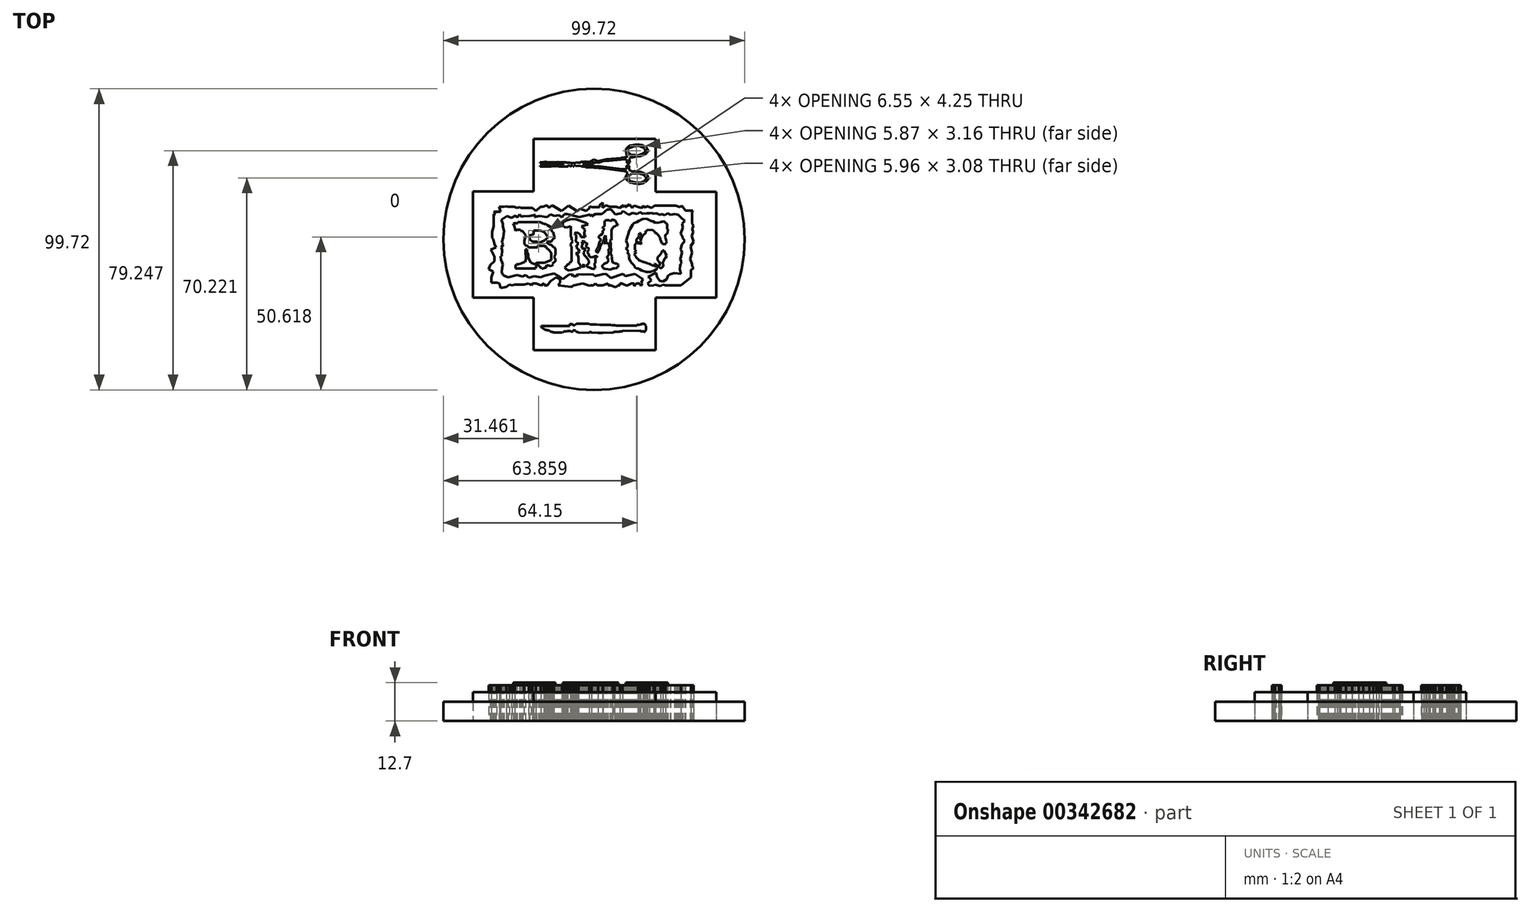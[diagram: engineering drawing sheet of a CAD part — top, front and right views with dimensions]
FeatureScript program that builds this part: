
annotation { "Feature Type Name" : "Feature", "Feature Type Description" : "" }
export const myFeature = defineFeature(function(context is Context, id is Id, definition is map)
    precondition{}
    {
        {
            var Q0;
            Q0=qCreatedBy(makeId("Top.planeOp"),FACE);
            var sketch = newSketch(context, id + "F0", { "sketchPlane" : qUnion([Q0])});
            skCircle(sketch, "E0", {"center": v(0, 0) * mm, "radius": 49.86 * mm});
            skSolve(sketch);
        }
        {
            var Q0;
            Q0=qCreatedBy(makeId("Top.planeOp"),FACE);
            var sketch = newSketch(context, id + "F1", { "sketchPlane" : qUnion([Q0])});
            skLineSegment(sketch, "E1", {"start": v(-40.1, 15.85) * mm, "end": v(-20.03, 15.85) * mm});
            skLineSegment(sketch, "E2", {"start": v(-20.03, 15.85) * mm, "end": v(-20.03, 33.22) * mm});
            skLineSegment(sketch, "E3", {"start": v(-20.03, 33.22) * mm, "end": v(20.4, 33.22) * mm});
            skLineSegment(sketch, "E4", {"start": v(20.4, 33.22) * mm, "end": v(20.4, 15.76) * mm});
            skLineSegment(sketch, "E5", {"start": v(20.4, 15.76) * mm, "end": v(40.46, 15.76) * mm});
            skLineSegment(sketch, "E6", {"start": v(40.46, 15.76) * mm, "end": v(40.46, -19.25) * mm});
            skLineSegment(sketch, "E7", {"start": v(40.46, -19.25) * mm, "end": v(20.4, -19.25) * mm});
            skLineSegment(sketch, "E8", {"start": v(20.4, -19.25) * mm, "end": v(20.4, -36.7) * mm});
            skLineSegment(sketch, "E9", {"start": v(20.4, -36.7) * mm, "end": v(-20.03, -36.7) * mm});
            skLineSegment(sketch, "E10", {"start": v(-20.03, -36.7) * mm, "end": v(-20.03, -19.25) * mm});
            skLineSegment(sketch, "E11", {"start": v(-20.03, -19.25) * mm, "end": v(-40.05, -19.25) * mm});
            skLineSegment(sketch, "E12", {"start": v(-40.05, -19.25) * mm, "end": v(-40.1, 15.85) * mm});
            skSolve(sketch);
        }
        {
            var Q0;
            Q0=qCreatedBy(makeId("Top.planeOp"),FACE);
            var sketch = newSketch(context, id + "F2", { "sketchPlane" : qUnion([Q0])});
            skLineSegment(sketch, "E13", {"start": v(-17.84, 25.58) * mm, "end": v(-17.84, 25.27) * mm});
            skLineSegment(sketch, "E14", {"start": v(-17.84, 25.27) * mm, "end": v(-16.2, 25.27) * mm});
            skLineSegment(sketch, "E15", {"start": v(-16.2, 25.27) * mm, "end": v(-16.2, 25.13) * mm});
            skLineSegment(sketch, "E16", {"start": v(-16.2, 25.13) * mm, "end": v(-15.9, 25.13) * mm});
            skLineSegment(sketch, "E17", {"start": v(-15.9, 25.13) * mm, "end": v(-15.76, 25.27) * mm});
            skLineSegment(sketch, "E18", {"start": v(-15.76, 25.27) * mm, "end": v(-15.26, 25.27) * mm});
            skLineSegment(sketch, "E19", {"start": v(-15.26, 25.27) * mm, "end": v(-15.26, 25.13) * mm});
            skLineSegment(sketch, "E20", {"start": v(-15.26, 25.13) * mm, "end": v(-12.92, 25.13) * mm});
            skLineSegment(sketch, "E21", {"start": v(-12.92, 25.13) * mm, "end": v(-12.8, 25) * mm});
            skLineSegment(sketch, "E22", {"start": v(-12.8, 25) * mm, "end": v(-12.56, 25) * mm});
            skLineSegment(sketch, "E23", {"start": v(-12.56, 25) * mm, "end": v(-12.56, 25.13) * mm});
            skLineSegment(sketch, "E24", {"start": v(-12.56, 25.13) * mm, "end": v(-12.27, 25) * mm});
            skLineSegment(sketch, "E25", {"start": v(-12.27, 25) * mm, "end": v(-12.15, 25) * mm});
            skLineSegment(sketch, "E26", {"start": v(-12.15, 25) * mm, "end": v(-9.99, 25) * mm});
            skLineSegment(sketch, "E27", {"start": v(-9.99, 25) * mm, "end": v(-9.99, 24.86) * mm});
            skLineSegment(sketch, "E28", {"start": v(-9.99, 24.86) * mm, "end": v(-10.34, 24.86) * mm});
            skLineSegment(sketch, "E29", {"start": v(-10.34, 24.86) * mm, "end": v(-11.16, 24.7) * mm});
            skLineSegment(sketch, "E30", {"start": v(-11.16, 24.7) * mm, "end": v(-11.19, 24.85) * mm});
            skLineSegment(sketch, "E31", {"start": v(-11.19, 24.85) * mm, "end": v(-11.41, 24.8) * mm});
            skLineSegment(sketch, "E32", {"start": v(-11.41, 24.8) * mm, "end": v(-11.86, 24.7) * mm});
            skLineSegment(sketch, "E33", {"start": v(-11.86, 24.7) * mm, "end": v(-11.89, 24.8) * mm});
            skLineSegment(sketch, "E34", {"start": v(-11.89, 24.8) * mm, "end": v(-12.03, 24.77) * mm});
            skLineSegment(sketch, "E35", {"start": v(-12.03, 24.77) * mm, "end": v(-12.56, 24.77) * mm});
            skLineSegment(sketch, "E36", {"start": v(-12.56, 24.77) * mm, "end": v(-12.8, 24.77) * mm});
            skLineSegment(sketch, "E37", {"start": v(-12.8, 24.77) * mm, "end": v(-12.8, 24.54) * mm});
            skLineSegment(sketch, "E38", {"start": v(-12.8, 24.54) * mm, "end": v(-13.2, 24.54) * mm});
            skLineSegment(sketch, "E39", {"start": v(-13.2, 24.54) * mm, "end": v(-13.2, 24.7) * mm});
            skLineSegment(sketch, "E40", {"start": v(-13.2, 24.7) * mm, "end": v(-13.43, 24.7) * mm});
            skLineSegment(sketch, "E41", {"start": v(-14.94, 24.58) * mm, "end": v(-13.43, 24.7) * mm});
            skLineSegment(sketch, "E42", {"start": v(-15.14, 24.58) * mm, "end": v(-14.94, 24.58) * mm});
            skLineSegment(sketch, "E43", {"start": v(-15.14, 24.58) * mm, "end": v(-15.13, 24.4) * mm});
            skLineSegment(sketch, "E44", {"start": v(-15.13, 24.4) * mm, "end": v(-15.3, 24.4) * mm});
            skLineSegment(sketch, "E45", {"start": v(-15.3, 24.4) * mm, "end": v(-15.31, 24.58) * mm});
            skLineSegment(sketch, "E46", {"start": v(-15.31, 24.58) * mm, "end": v(-15.58, 24.56) * mm});
            skLineSegment(sketch, "E47", {"start": v(-15.58, 24.56) * mm, "end": v(-15.57, 24.4) * mm});
            skLineSegment(sketch, "E48", {"start": v(-15.57, 24.4) * mm, "end": v(-15.9, 24.37) * mm});
            skLineSegment(sketch, "E49", {"start": v(-15.9, 24.37) * mm, "end": v(-15.92, 24.58) * mm});
            skLineSegment(sketch, "E50", {"start": v(-15.92, 24.58) * mm, "end": v(-16.2, 24.56) * mm});
            skLineSegment(sketch, "E51", {"start": v(-16.2, 24.56) * mm, "end": v(-16.34, 24.4) * mm});
            skLineSegment(sketch, "E52", {"start": v(-16.34, 24.4) * mm, "end": v(-17.87, 24.4) * mm});
            skLineSegment(sketch, "E53", {"start": v(-17.87, 24.4) * mm, "end": v(-17.84, 24.11) * mm});
            skLineSegment(sketch, "E54", {"start": v(-17.84, 24.11) * mm, "end": v(-15.14, 24.11) * mm});
            skLineSegment(sketch, "E55", {"start": v(-15.14, 24.11) * mm, "end": v(-14.67, 24.15) * mm});
            skLineSegment(sketch, "E56", {"start": v(-14.67, 24.15) * mm, "end": v(-14.53, 24.11) * mm});
            skLineSegment(sketch, "E57", {"start": v(-14.53, 24.11) * mm, "end": v(-14.12, 24.11) * mm});
            skLineSegment(sketch, "E58", {"start": v(-14.12, 24.11) * mm, "end": v(-13.84, 24.13) * mm});
            skLineSegment(sketch, "E59", {"start": v(-13.84, 24.13) * mm, "end": v(-12.97, 24.2) * mm});
            skLineSegment(sketch, "E60", {"start": v(-12.97, 24.2) * mm, "end": v(-12.56, 24.11) * mm});
            skLineSegment(sketch, "E61", {"start": v(-12.56, 24.11) * mm, "end": v(-12.39, 24.2) * mm});
            skLineSegment(sketch, "E62", {"start": v(-12.39, 24.2) * mm, "end": v(-11.57, 24.27) * mm});
            skLineSegment(sketch, "E63", {"start": v(-11.57, 24.27) * mm, "end": v(-11.56, 24.11) * mm});
            skLineSegment(sketch, "E64", {"start": v(-11.56, 24.11) * mm, "end": v(-11.29, 24.13) * mm});
            skLineSegment(sketch, "E65", {"start": v(-11.29, 24.13) * mm, "end": v(-11.16, 24.14) * mm});
            skLineSegment(sketch, "E66", {"start": v(-11.16, 24.14) * mm, "end": v(-8.61, 24.14) * mm});
            skLineSegment(sketch, "E67", {"start": v(-8.61, 24.14) * mm, "end": v(-8.61, 24.42) * mm});
            skLineSegment(sketch, "E68", {"start": v(-8.61, 24.42) * mm, "end": v(-8.03, 24.47) * mm});
            skLineSegment(sketch, "E69", {"start": v(-8.03, 24.47) * mm, "end": v(-8, 24.2) * mm});
            skLineSegment(sketch, "E70", {"start": v(-8, 24.2) * mm, "end": v(-7.59, 24.23) * mm});
            skLineSegment(sketch, "E71", {"start": v(-7.59, 24.23) * mm, "end": v(-7.6, 24.42) * mm});
            skLineSegment(sketch, "E72", {"start": v(-7.6, 24.42) * mm, "end": v(-6.99, 24.47) * mm});
            skLineSegment(sketch, "E73", {"start": v(-6.99, 24.47) * mm, "end": v(-6.96, 24.13) * mm});
            skLineSegment(sketch, "E74", {"start": v(-6.96, 24.13) * mm, "end": v(-6.64, 24.16) * mm});
            skLineSegment(sketch, "E75", {"start": v(-6.64, 24.16) * mm, "end": v(-6.67, 24.47) * mm});
            skLineSegment(sketch, "E76", {"start": v(-6.67, 24.47) * mm, "end": v(-6.1, 24.51) * mm});
            skLineSegment(sketch, "E77", {"start": v(-6.1, 24.51) * mm, "end": v(-6.08, 24.2) * mm});
            skLineSegment(sketch, "E78", {"start": v(-6.08, 24.2) * mm, "end": v(-4.47, 24.33) * mm});
            skLineSegment(sketch, "E79", {"start": v(-4.47, 24.33) * mm, "end": v(-4.1, 24.11) * mm});
            skLineSegment(sketch, "E80", {"start": v(-4.1, 24.11) * mm, "end": v(-3.34, 24.17) * mm});
            skLineSegment(sketch, "E81", {"start": v(-3.34, 24.17) * mm, "end": v(-2.81, 24.11) * mm});
            skLineSegment(sketch, "E82", {"start": v(-2.81, 24.11) * mm, "end": v(-2.25, 23.79) * mm});
            skLineSegment(sketch, "E83", {"start": v(-2.25, 23.79) * mm, "end": v(-1.73, 23.94) * mm});
            skLineSegment(sketch, "E84", {"start": v(-1.73, 23.94) * mm, "end": v(3.2, 23.51) * mm});
            skLineSegment(sketch, "E85", {"start": v(3.2, 23.51) * mm, "end": v(10.9, 22.47) * mm});
            skLineSegment(sketch, "E86", {"start": v(10.9, 22.47) * mm, "end": v(10.95, 21.79) * mm});
            skLineSegment(sketch, "E87", {"start": v(10.95, 21.79) * mm, "end": v(10.97, 21.58) * mm});
            skLineSegment(sketch, "E88", {"start": v(10.95, 21.4) * mm, "end": v(10.97, 21.58) * mm});
            skLineSegment(sketch, "E89", {"start": v(10.95, 21.4) * mm, "end": v(10.63, 21.17) * mm});
            skLineSegment(sketch, "E90", {"start": v(10.63, 21.17) * mm, "end": v(10.65, 20.91) * mm});
            skLineSegment(sketch, "E91", {"start": v(10.65, 20.91) * mm, "end": v(10.57, 20.78) * mm});
            skLineSegment(sketch, "E92", {"start": v(10.57, 20.78) * mm, "end": v(10.47, 20.6) * mm});
            skLineSegment(sketch, "E93", {"start": v(10.47, 20.6) * mm, "end": v(10.49, 20.35) * mm});
            skLineSegment(sketch, "E94", {"start": v(10.49, 20.35) * mm, "end": v(10.73, 19.85) * mm});
            skLineSegment(sketch, "E95", {"start": v(10.73, 19.85) * mm, "end": v(11.48, 19.2) * mm});
            skLineSegment(sketch, "E96", {"start": v(11.48, 19.2) * mm, "end": v(12.13, 18.83) * mm});
            skLineSegment(sketch, "E97", {"start": v(12.13, 18.83) * mm, "end": v(13.3, 18.5) * mm});
            skLineSegment(sketch, "E98", {"start": v(13.3, 18.5) * mm, "end": v(14.8, 18.32) * mm});
            skLineSegment(sketch, "E99", {"start": v(14.8, 18.32) * mm, "end": v(16.04, 18.5) * mm});
            skLineSegment(sketch, "E100", {"start": v(16.04, 18.5) * mm, "end": v(17.27, 19.24) * mm});
            skLineSegment(sketch, "E101", {"start": v(17.27, 19.24) * mm, "end": v(17.88, 19.85) * mm});
            skLineSegment(sketch, "E102", {"start": v(17.88, 19.85) * mm, "end": v(17.98, 20.07) * mm});
            skLineSegment(sketch, "E103", {"start": v(17.98, 20.07) * mm, "end": v(18.03, 20.2) * mm});
            skLineSegment(sketch, "E104", {"start": v(18.03, 20.2) * mm, "end": v(17.85, 20.76) * mm});
            skLineSegment(sketch, "E105", {"start": v(17.85, 20.76) * mm, "end": v(17.56, 21.29) * mm});
            skLineSegment(sketch, "E106", {"start": v(17.56, 21.29) * mm, "end": v(16.09, 22.14) * mm});
            skLineSegment(sketch, "E107", {"start": v(16.09, 22.14) * mm, "end": v(15.92, 22.1) * mm});
            skLineSegment(sketch, "E108", {"start": v(15.92, 22.1) * mm, "end": v(15.63, 22.23) * mm});
            skLineSegment(sketch, "E109", {"start": v(15.63, 22.23) * mm, "end": v(15.4, 22.34) * mm});
            skLineSegment(sketch, "E110", {"start": v(15.4, 22.34) * mm, "end": v(15.22, 22.37) * mm});
            skLineSegment(sketch, "E111", {"start": v(15.22, 22.37) * mm, "end": v(14.23, 22.47) * mm});
            skLineSegment(sketch, "E112", {"start": v(14.23, 22.47) * mm, "end": v(13.87, 22.47) * mm});
            skLineSegment(sketch, "E113", {"start": v(13.87, 22.47) * mm, "end": v(13.34, 22.6) * mm});
            skLineSegment(sketch, "E114", {"start": v(13.34, 22.6) * mm, "end": v(12.58, 22.47) * mm});
            skLineSegment(sketch, "E115", {"start": v(12.58, 22.47) * mm, "end": v(12.52, 22.58) * mm});
            skLineSegment(sketch, "E116", {"start": v(12.52, 22.58) * mm, "end": v(12.46, 22.7) * mm});
            skLineSegment(sketch, "E117", {"start": v(12.46, 22.7) * mm, "end": v(12.12, 22.67) * mm});
            skLineSegment(sketch, "E118", {"start": v(12.12, 22.67) * mm, "end": v(11.64, 23.1) * mm});
            skLineSegment(sketch, "E119", {"start": v(11.64, 23.1) * mm, "end": v(11.64, 24.33) * mm});
            skLineSegment(sketch, "E120", {"start": v(11.64, 24.33) * mm, "end": v(11.3, 24.53) * mm});
            skLineSegment(sketch, "E121", {"start": v(11.3, 24.53) * mm, "end": v(10.97, 24.5) * mm});
            skLineSegment(sketch, "E122", {"start": v(10.97, 24.5) * mm, "end": v(10.79, 24.2) * mm});
            skLineSegment(sketch, "E123", {"start": v(10.79, 24.2) * mm, "end": v(10.85, 23.41) * mm});
            skLineSegment(sketch, "E124", {"start": v(10.85, 23.41) * mm, "end": v(10.65, 23.49) * mm});
            skLineSegment(sketch, "E125", {"start": v(10.65, 23.49) * mm, "end": v(10.53, 23.28) * mm});
            skLineSegment(sketch, "E126", {"start": v(10.53, 23.28) * mm, "end": v(10.38, 23.28) * mm});
            skLineSegment(sketch, "E127", {"start": v(10.38, 23.28) * mm, "end": v(9.3, 23.2) * mm});
            skLineSegment(sketch, "E128", {"start": v(9.3, 23.2) * mm, "end": v(1.17, 24.2) * mm});
            skLineSegment(sketch, "E129", {"start": v(1.17, 24.2) * mm, "end": v(0.02, 24.11) * mm});
            skLineSegment(sketch, "E130", {"start": v(0.02, 24.11) * mm, "end": v(0, 24.33) * mm});
            skLineSegment(sketch, "E131", {"start": v(0, 24.33) * mm, "end": v(-0.25, 24.47) * mm});
            skLineSegment(sketch, "E132", {"start": v(-0.25, 24.47) * mm, "end": v(-2.08, 24.58) * mm});
            skLineSegment(sketch, "E133", {"start": v(-2.08, 24.58) * mm, "end": v(-2.6, 24.64) * mm});
            skLineSegment(sketch, "E134", {"start": v(-2.6, 24.64) * mm, "end": v(-2.82, 24.77) * mm});
            skLineSegment(sketch, "E135", {"start": v(-2.82, 24.77) * mm, "end": v(-3.17, 24.74) * mm});
            skLineSegment(sketch, "E136", {"start": v(-3.17, 24.74) * mm, "end": v(-3.8, 25) * mm});
            skLineSegment(sketch, "E137", {"start": v(-3.8, 25) * mm, "end": v(-2.9, 25.06) * mm});
            skLineSegment(sketch, "E138", {"start": v(-2.9, 25.06) * mm, "end": v(-1.6, 25.18) * mm});
            skLineSegment(sketch, "E139", {"start": v(-1.6, 25.18) * mm, "end": v(-1.32, 25.32) * mm});
            skLineSegment(sketch, "E140", {"start": v(-1.32, 25.32) * mm, "end": v(-0.37, 25.43) * mm});
            skLineSegment(sketch, "E141", {"start": v(-0.37, 25.43) * mm, "end": v(0.27, 25.46) * mm});
            skLineSegment(sketch, "E142", {"start": v(0.27, 25.46) * mm, "end": v(0.72, 25.6) * mm});
            skLineSegment(sketch, "E143", {"start": v(0.72, 25.6) * mm, "end": v(1.53, 25.46) * mm});
            skLineSegment(sketch, "E144", {"start": v(1.53, 25.46) * mm, "end": v(2.25, 25.64) * mm});
            skLineSegment(sketch, "E145", {"start": v(2.25, 25.64) * mm, "end": v(3.02, 25.86) * mm});
            skLineSegment(sketch, "E146", {"start": v(3.02, 25.86) * mm, "end": v(4.96, 26.04) * mm});
            skLineSegment(sketch, "E147", {"start": v(4.96, 26.04) * mm, "end": v(10.32, 26.5) * mm});
            skLineSegment(sketch, "E148", {"start": v(10.32, 26.5) * mm, "end": v(10.84, 26.22) * mm});
            skLineSegment(sketch, "E149", {"start": v(10.84, 26.22) * mm, "end": v(10.84, 25.46) * mm});
            skLineSegment(sketch, "E150", {"start": v(10.84, 25.46) * mm, "end": v(11.2, 25.1) * mm});
            skLineSegment(sketch, "E151", {"start": v(11.2, 25.1) * mm, "end": v(11.83, 25.36) * mm});
            skLineSegment(sketch, "E152", {"start": v(11.83, 25.36) * mm, "end": v(11.67, 26.72) * mm});
            skLineSegment(sketch, "E153", {"start": v(11.67, 26.72) * mm, "end": v(11.83, 26.97) * mm});
            skLineSegment(sketch, "E154", {"start": v(11.83, 26.97) * mm, "end": v(11.94, 27.08) * mm});
            skLineSegment(sketch, "E155", {"start": v(11.94, 27.08) * mm, "end": v(12.2, 27.22) * mm});
            skLineSegment(sketch, "E156", {"start": v(12.2, 27.22) * mm, "end": v(12.78, 27.22) * mm});
            skLineSegment(sketch, "E157", {"start": v(12.78, 27.22) * mm, "end": v(13.36, 27.3) * mm});
            skLineSegment(sketch, "E158", {"start": v(13.36, 27.3) * mm, "end": v(14.32, 27.38) * mm});
            skLineSegment(sketch, "E159", {"start": v(14.32, 27.38) * mm, "end": v(15.05, 27.53) * mm});
            skLineSegment(sketch, "E160", {"start": v(15.05, 27.53) * mm, "end": v(15.33, 27.55) * mm});
            skLineSegment(sketch, "E161", {"start": v(15.33, 27.55) * mm, "end": v(15.52, 27.64) * mm});
            skLineSegment(sketch, "E162", {"start": v(15.52, 27.64) * mm, "end": v(16.3, 27.93) * mm});
            skLineSegment(sketch, "E163", {"start": v(16.3, 27.93) * mm, "end": v(16.45, 28.02) * mm});
            skLineSegment(sketch, "E164", {"start": v(16.45, 28.02) * mm, "end": v(16.58, 28.1) * mm});
            skLineSegment(sketch, "E165", {"start": v(16.58, 28.1) * mm, "end": v(17.17, 28.41) * mm});
            skLineSegment(sketch, "E166", {"start": v(17.17, 28.41) * mm, "end": v(17.3, 28.51) * mm});
            skLineSegment(sketch, "E167", {"start": v(17.3, 28.51) * mm, "end": v(17.67, 28.99) * mm});
            skLineSegment(sketch, "E168", {"start": v(17.67, 28.99) * mm, "end": v(17.81, 29.23) * mm});
            skLineSegment(sketch, "E169", {"start": v(17.81, 29.23) * mm, "end": v(17.82, 29.45) * mm});
            skLineSegment(sketch, "E170", {"start": v(17.82, 29.45) * mm, "end": v(17.17, 30.56) * mm});
            skLineSegment(sketch, "E171", {"start": v(17.17, 30.56) * mm, "end": v(17.06, 30.67) * mm});
            skLineSegment(sketch, "E172", {"start": v(17.06, 30.67) * mm, "end": v(16.87, 30.77) * mm});
            skLineSegment(sketch, "E173", {"start": v(16.87, 30.77) * mm, "end": v(16.68, 30.9) * mm});
            skLineSegment(sketch, "E174", {"start": v(16.68, 30.9) * mm, "end": v(16.37, 31.08) * mm});
            skLineSegment(sketch, "E175", {"start": v(16.37, 31.08) * mm, "end": v(16.23, 31.13) * mm});
            skLineSegment(sketch, "E176", {"start": v(16.23, 31.13) * mm, "end": v(16, 31.18) * mm});
            skLineSegment(sketch, "E177", {"start": v(16, 31.18) * mm, "end": v(15.8, 31.28) * mm});
            skLineSegment(sketch, "E178", {"start": v(15.8, 31.28) * mm, "end": v(15.5, 31.23) * mm});
            skLineSegment(sketch, "E179", {"start": v(15.5, 31.23) * mm, "end": v(15.2, 31.28) * mm});
            skLineSegment(sketch, "E180", {"start": v(15.2, 31.28) * mm, "end": v(14.87, 31.35) * mm});
            skLineSegment(sketch, "E181", {"start": v(14.87, 31.35) * mm, "end": v(14.74, 31.43) * mm});
            skLineSegment(sketch, "E182", {"start": v(14.74, 31.43) * mm, "end": v(13.85, 31.38) * mm});
            skLineSegment(sketch, "E183", {"start": v(13.85, 31.38) * mm, "end": v(13.62, 31.33) * mm});
            skLineSegment(sketch, "E184", {"start": v(13.62, 31.33) * mm, "end": v(13.3, 31.3) * mm});
            skLineSegment(sketch, "E185", {"start": v(13.3, 31.3) * mm, "end": v(13.07, 31.3) * mm});
            skLineSegment(sketch, "E186", {"start": v(13.07, 31.3) * mm, "end": v(12.73, 31.17) * mm});
            skLineSegment(sketch, "E187", {"start": v(12.73, 31.17) * mm, "end": v(12.4, 31.14) * mm});
            skLineSegment(sketch, "E188", {"start": v(12.4, 31.14) * mm, "end": v(12.17, 31.12) * mm});
            skLineSegment(sketch, "E189", {"start": v(12.17, 31.12) * mm, "end": v(11.53, 30.72) * mm});
            skLineSegment(sketch, "E190", {"start": v(11.53, 30.72) * mm, "end": v(11.2, 30.58) * mm});
            skLineSegment(sketch, "E191", {"start": v(11.2, 30.58) * mm, "end": v(11.07, 30.5) * mm});
            skLineSegment(sketch, "E192", {"start": v(11.07, 30.5) * mm, "end": v(10.73, 30.12) * mm});
            skLineSegment(sketch, "E193", {"start": v(10.73, 30.12) * mm, "end": v(10.56, 29.77) * mm});
            skLineSegment(sketch, "E194", {"start": v(10.56, 29.77) * mm, "end": v(10.45, 29.52) * mm});
            skLineSegment(sketch, "E195", {"start": v(10.45, 29.52) * mm, "end": v(10.46, 29.36) * mm});
            skLineSegment(sketch, "E196", {"start": v(10.46, 29.36) * mm, "end": v(10.52, 29.22) * mm});
            skLineSegment(sketch, "E197", {"start": v(10.52, 29.22) * mm, "end": v(10.56, 29) * mm});
            skLineSegment(sketch, "E198", {"start": v(10.56, 29) * mm, "end": v(10.52, 28.82) * mm});
            skLineSegment(sketch, "E199", {"start": v(10.52, 28.82) * mm, "end": v(10.72, 28.55) * mm});
            skLineSegment(sketch, "E200", {"start": v(10.72, 28.55) * mm, "end": v(10.79, 27.95) * mm});
            skLineSegment(sketch, "E201", {"start": v(10.79, 27.95) * mm, "end": v(11.06, 27.73) * mm});
            skLineSegment(sketch, "E202", {"start": v(11.06, 27.73) * mm, "end": v(11.1, 27.64) * mm});
            skLineSegment(sketch, "E203", {"start": v(11.1, 27.64) * mm, "end": v(10.67, 27.2) * mm});
            skLineSegment(sketch, "E204", {"start": v(10.67, 27.2) * mm, "end": v(10.07, 27.22) * mm});
            skLineSegment(sketch, "E205", {"start": v(10.07, 27.22) * mm, "end": v(10, 27.08) * mm});
            skLineSegment(sketch, "E206", {"start": v(10, 27.08) * mm, "end": v(9.13, 27.08) * mm});
            skLineSegment(sketch, "E207", {"start": v(9.13, 27.08) * mm, "end": v(8.94, 26.9) * mm});
            skLineSegment(sketch, "E208", {"start": v(8.94, 26.9) * mm, "end": v(4.28, 26.5) * mm});
            skLineSegment(sketch, "E209", {"start": v(4.28, 26.5) * mm, "end": v(4.27, 26.47) * mm});
            skLineSegment(sketch, "E210", {"start": v(4.27, 26.47) * mm, "end": v(4.15, 26.47) * mm});
            skLineSegment(sketch, "E211", {"start": v(4.15, 26.47) * mm, "end": v(4.27, 26.5) * mm});
            skLineSegment(sketch, "E212", {"start": v(4.27, 26.5) * mm, "end": v(1.36, 25.96) * mm});
            skLineSegment(sketch, "E213", {"start": v(1.36, 25.96) * mm, "end": v(0, 26.47) * mm});
            skLineSegment(sketch, "E214", {"start": v(0, 26.47) * mm, "end": v(-1.23, 25.82) * mm});
            skLineSegment(sketch, "E215", {"start": v(-1.23, 25.82) * mm, "end": v(-2.59, 25.64) * mm});
            skLineSegment(sketch, "E216", {"start": v(-2.59, 25.64) * mm, "end": v(-2.97, 25.73) * mm});
            skLineSegment(sketch, "E217", {"start": v(-2.97, 25.73) * mm, "end": v(-3.7, 25.64) * mm});
            skLineSegment(sketch, "E218", {"start": v(-3.7, 25.64) * mm, "end": v(-4.24, 25.69) * mm});
            skLineSegment(sketch, "E219", {"start": v(-4.24, 25.69) * mm, "end": v(-4.96, 25.27) * mm});
            skLineSegment(sketch, "E220", {"start": v(-4.96, 25.27) * mm, "end": v(-5.5, 25.5) * mm});
            skLineSegment(sketch, "E221", {"start": v(-5.5, 25.5) * mm, "end": v(-6.45, 25.33) * mm});
            skLineSegment(sketch, "E222", {"start": v(-6.45, 25.33) * mm, "end": v(-6.95, 25.28) * mm});
            skLineSegment(sketch, "E223", {"start": v(-6.95, 25.28) * mm, "end": v(-7.67, 25.28) * mm});
            skLineSegment(sketch, "E224", {"start": v(-7.67, 25.28) * mm, "end": v(-8, 25.46) * mm});
            skLineSegment(sketch, "E225", {"start": v(-8, 25.46) * mm, "end": v(-8.3, 25.46) * mm});
            skLineSegment(sketch, "E226", {"start": v(-8.3, 25.46) * mm, "end": v(-8.48, 25.42) * mm});
            skLineSegment(sketch, "E227", {"start": v(-8.48, 25.42) * mm, "end": v(-8.94, 25.37) * mm});
            skLineSegment(sketch, "E228", {"start": v(-8.94, 25.37) * mm, "end": v(-9.3, 25.5) * mm});
            skLineSegment(sketch, "E229", {"start": v(-11.92, 25.64) * mm, "end": v(-9.3, 25.5) * mm});
            skLineSegment(sketch, "E230", {"start": v(-11.92, 25.64) * mm, "end": v(-15.76, 25.5) * mm});
            skLineSegment(sketch, "E231", {"start": v(-15.76, 25.5) * mm, "end": v(-15.76, 25.64) * mm});
            skLineSegment(sketch, "E232", {"start": v(-15.76, 25.64) * mm, "end": v(-16.34, 25.82) * mm});
            skLineSegment(sketch, "E233", {"start": v(-16.34, 25.82) * mm, "end": v(-16.43, 25.7) * mm});
            skLineSegment(sketch, "E234", {"start": v(-16.43, 25.7) * mm, "end": v(-17.84, 25.58) * mm});
            skLineSegment(sketch, "E235", {"start": v(4.27, 26.47) * mm, "end": v(4.24, 26.49) * mm});
            skLineSegment(sketch, "E236", {"start": v(11.33, 28.87) * mm, "end": v(11.09, 29.1) * mm});
            skLineSegment(sketch, "E237", {"start": v(11.09, 29.1) * mm, "end": v(11.06, 29.6) * mm});
            skLineSegment(sketch, "E238", {"start": v(11.06, 29.6) * mm, "end": v(11.24, 30) * mm});
            skLineSegment(sketch, "E239", {"start": v(11.24, 30) * mm, "end": v(11.52, 30.22) * mm});
            skLineSegment(sketch, "E240", {"start": v(11.52, 30.22) * mm, "end": v(11.97, 30.34) * mm});
            skLineSegment(sketch, "E241", {"start": v(11.97, 30.34) * mm, "end": v(12.42, 30.54) * mm});
            skLineSegment(sketch, "E242", {"start": v(12.42, 30.54) * mm, "end": v(12.87, 30.72) * mm});
            skLineSegment(sketch, "E243", {"start": v(12.87, 30.72) * mm, "end": v(13.19, 30.72) * mm});
            skLineSegment(sketch, "E244", {"start": v(13.19, 30.72) * mm, "end": v(13.95, 30.85) * mm});
            skLineSegment(sketch, "E245", {"start": v(13.95, 30.85) * mm, "end": v(14.25, 30.95) * mm});
            skLineSegment(sketch, "E246", {"start": v(14.25, 30.95) * mm, "end": v(14.8, 30.97) * mm});
            skLineSegment(sketch, "E247", {"start": v(14.8, 30.97) * mm, "end": v(15.24, 30.85) * mm});
            skLineSegment(sketch, "E248", {"start": v(15.24, 30.85) * mm, "end": v(15.67, 30.63) * mm});
            skLineSegment(sketch, "E249", {"start": v(15.67, 30.63) * mm, "end": v(16.12, 30.54) * mm});
            skLineSegment(sketch, "E250", {"start": v(16.12, 30.54) * mm, "end": v(16.6, 30.31) * mm});
            skLineSegment(sketch, "E251", {"start": v(16.6, 30.31) * mm, "end": v(16.7, 30.18) * mm});
            skLineSegment(sketch, "E252", {"start": v(16.7, 30.18) * mm, "end": v(16.9, 29.88) * mm});
            skLineSegment(sketch, "E253", {"start": v(16.9, 29.88) * mm, "end": v(16.94, 29.34) * mm});
            skLineSegment(sketch, "E254", {"start": v(16.94, 29.34) * mm, "end": v(16.94, 29.14) * mm});
            skLineSegment(sketch, "E255", {"start": v(16.94, 29.14) * mm, "end": v(16.21, 28.46) * mm});
            skLineSegment(sketch, "E256", {"start": v(16.21, 28.46) * mm, "end": v(15.58, 28.23) * mm});
            skLineSegment(sketch, "E257", {"start": v(15.58, 28.23) * mm, "end": v(14.68, 27.8) * mm});
            skLineSegment(sketch, "E258", {"start": v(14.68, 27.8) * mm, "end": v(14.25, 27.83) * mm});
            skLineSegment(sketch, "E259", {"start": v(14.25, 27.83) * mm, "end": v(13.5, 27.92) * mm});
            skLineSegment(sketch, "E260", {"start": v(13.5, 27.92) * mm, "end": v(12.87, 27.92) * mm});
            skLineSegment(sketch, "E261", {"start": v(12.87, 27.92) * mm, "end": v(12.24, 27.96) * mm});
            skLineSegment(sketch, "E262", {"start": v(12.24, 27.96) * mm, "end": v(11.9, 28.33) * mm});
            skLineSegment(sketch, "E263", {"start": v(11.9, 28.33) * mm, "end": v(11.45, 28.5) * mm});
            skLineSegment(sketch, "E264", {"start": v(11.45, 28.5) * mm, "end": v(11.33, 28.87) * mm});
            skLineSegment(sketch, "E265", {"start": v(11.33, 20.63) * mm, "end": v(11.46, 21.02) * mm});
            skLineSegment(sketch, "E266", {"start": v(11.46, 21.02) * mm, "end": v(11.73, 21.3) * mm});
            skLineSegment(sketch, "E267", {"start": v(11.73, 21.3) * mm, "end": v(11.84, 21.18) * mm});
            skLineSegment(sketch, "E268", {"start": v(11.84, 21.18) * mm, "end": v(11.97, 21.4) * mm});
            skLineSegment(sketch, "E269", {"start": v(11.97, 21.4) * mm, "end": v(12.49, 21.75) * mm});
            skLineSegment(sketch, "E270", {"start": v(12.49, 21.75) * mm, "end": v(12.91, 21.85) * mm});
            skLineSegment(sketch, "E271", {"start": v(12.91, 21.85) * mm, "end": v(13.34, 21.82) * mm});
            skLineSegment(sketch, "E272", {"start": v(13.34, 21.82) * mm, "end": v(13.7, 21.9) * mm});
            skLineSegment(sketch, "E273", {"start": v(13.7, 21.9) * mm, "end": v(15.22, 21.75) * mm});
            skLineSegment(sketch, "E274", {"start": v(15.22, 21.75) * mm, "end": v(15.37, 21.67) * mm});
            skLineSegment(sketch, "E275", {"start": v(15.37, 21.67) * mm, "end": v(15.71, 21.5) * mm});
            skLineSegment(sketch, "E276", {"start": v(15.71, 21.5) * mm, "end": v(15.94, 21.54) * mm});
            skLineSegment(sketch, "E277", {"start": v(15.94, 21.54) * mm, "end": v(16.25, 21.4) * mm});
            skLineSegment(sketch, "E278", {"start": v(16.25, 21.4) * mm, "end": v(16.63, 21.2) * mm});
            skLineSegment(sketch, "E279", {"start": v(16.63, 21.2) * mm, "end": v(17.27, 20.55) * mm});
            skLineSegment(sketch, "E280", {"start": v(17.27, 20.55) * mm, "end": v(17.23, 20.3) * mm});
            skLineSegment(sketch, "E281", {"start": v(17.23, 20.3) * mm, "end": v(17.16, 20.04) * mm});
            skLineSegment(sketch, "E282", {"start": v(17.16, 20.04) * mm, "end": v(17.08, 19.81) * mm});
            skLineSegment(sketch, "E283", {"start": v(17.08, 19.81) * mm, "end": v(16.9, 19.57) * mm});
            skLineSegment(sketch, "E284", {"start": v(16.9, 19.57) * mm, "end": v(16.66, 19.34) * mm});
            skLineSegment(sketch, "E285", {"start": v(16.66, 19.34) * mm, "end": v(16.47, 19.18) * mm});
            skLineSegment(sketch, "E286", {"start": v(16.47, 19.18) * mm, "end": v(16.13, 19.03) * mm});
            skLineSegment(sketch, "E287", {"start": v(16.13, 19.03) * mm, "end": v(15.8, 18.9) * mm});
            skLineSegment(sketch, "E288", {"start": v(15.8, 18.9) * mm, "end": v(15.41, 18.85) * mm});
            skLineSegment(sketch, "E289", {"start": v(15.41, 18.85) * mm, "end": v(13.7, 18.82) * mm});
            skLineSegment(sketch, "E290", {"start": v(13.7, 18.82) * mm, "end": v(13.47, 18.97) * mm});
            skLineSegment(sketch, "E291", {"start": v(13.47, 18.97) * mm, "end": v(12.95, 19.03) * mm});
            skLineSegment(sketch, "E292", {"start": v(12.95, 19.03) * mm, "end": v(12.8, 19.1) * mm});
            skLineSegment(sketch, "E293", {"start": v(12.8, 19.1) * mm, "end": v(12.45, 19.13) * mm});
            skLineSegment(sketch, "E294", {"start": v(12.45, 19.13) * mm, "end": v(12.22, 19.34) * mm});
            skLineSegment(sketch, "E295", {"start": v(12.22, 19.34) * mm, "end": v(12, 19.34) * mm});
            skLineSegment(sketch, "E296", {"start": v(12, 19.34) * mm, "end": v(11.73, 19.61) * mm});
            skLineSegment(sketch, "E297", {"start": v(11.73, 19.61) * mm, "end": v(11.46, 19.88) * mm});
            skLineSegment(sketch, "E298", {"start": v(11.46, 19.88) * mm, "end": v(11.35, 20.2) * mm});
            skLineSegment(sketch, "E299", {"start": v(11.35, 20.2) * mm, "end": v(11.3, 20.47) * mm});
            skLineSegment(sketch, "E300", {"start": v(11.3, 20.47) * mm, "end": v(11.33, 20.63) * mm});
            skSolve(sketch);
        }
        {
            var Q0;
            Q0=qCreatedBy(makeId("Top.planeOp"),FACE);
            var sketch = newSketch(context, id + "F3", { "sketchPlane" : qUnion([Q0])});
            skLineSegment(sketch, "E301", {"start": v(16.23, -13.23) * mm, "end": v(15.54, -14.34) * mm});
            skLineSegment(sketch, "E302", {"start": v(15.54, -14.34) * mm, "end": v(16.02, -14.64) * mm});
            skLineSegment(sketch, "E303", {"start": v(16.02, -14.64) * mm, "end": v(15.54, -15.4) * mm});
            skLineSegment(sketch, "E304", {"start": v(14.05, -14.64) * mm, "end": v(13.23, -15.44) * mm});
            skLineSegment(sketch, "E305", {"start": v(13.23, -15.44) * mm, "end": v(13.23, -14.64) * mm});
            skLineSegment(sketch, "E306", {"start": v(13.23, -14.64) * mm, "end": v(12.35, -14.64) * mm});
            skLineSegment(sketch, "E307", {"start": v(12.35, -14.64) * mm, "end": v(10.85, -15.34) * mm});
            skLineSegment(sketch, "E308", {"start": v(10.85, -15.34) * mm, "end": v(9.17, -14.64) * mm});
            skLineSegment(sketch, "E309", {"start": v(9.17, -14.64) * mm, "end": v(8.52, -14.64) * mm});
            skLineSegment(sketch, "E310", {"start": v(8.52, -14.64) * mm, "end": v(8.52, -15.25) * mm});
            skLineSegment(sketch, "E311", {"start": v(8.52, -15.25) * mm, "end": v(7.9, -15.25) * mm});
            skLineSegment(sketch, "E312", {"start": v(7.9, -15.25) * mm, "end": v(7.2, -15.93) * mm});
            skLineSegment(sketch, "E313", {"start": v(7.2, -15.93) * mm, "end": v(5.55, -15.25) * mm});
            skLineSegment(sketch, "E314", {"start": v(5.55, -15.25) * mm, "end": v(4.62, -15.25) * mm});
            skLineSegment(sketch, "E315", {"start": v(4.62, -15.25) * mm, "end": v(4.62, -14.64) * mm});
            skLineSegment(sketch, "E316", {"start": v(4.62, -14.64) * mm, "end": v(2.84, -15.25) * mm});
            skLineSegment(sketch, "E317", {"start": v(2.84, -15.25) * mm, "end": v(1.1, -15.25) * mm});
            skLineSegment(sketch, "E318", {"start": v(1.1, -15.25) * mm, "end": v(0.41, -14.64) * mm});
            skLineSegment(sketch, "E319", {"start": v(0.41, -14.64) * mm, "end": v(-0.13, -15.25) * mm});
            skLineSegment(sketch, "E320", {"start": v(-0.13, -15.25) * mm, "end": v(-1.1, -15.25) * mm});
            skLineSegment(sketch, "E321", {"start": v(-1.1, -15.25) * mm, "end": v(-1.51, -15.41) * mm});
            skLineSegment(sketch, "E322", {"start": v(-1.51, -15.41) * mm, "end": v(-3.7, -14.64) * mm});
            skLineSegment(sketch, "E323", {"start": v(-3.7, -14.64) * mm, "end": v(-6.63, -15.25) * mm});
            skLineSegment(sketch, "E324", {"start": v(-6.63, -15.25) * mm, "end": v(-7.52, -15.75) * mm});
            skLineSegment(sketch, "E325", {"start": v(-7.52, -15.75) * mm, "end": v(-11.9, -15.25) * mm});
            skLineSegment(sketch, "E326", {"start": v(-11.9, -15.25) * mm, "end": v(-11.19, -14.34) * mm});
            skLineSegment(sketch, "E327", {"start": v(-11.19, -14.34) * mm, "end": v(-11.19, -13.2) * mm});
            skLineSegment(sketch, "E328", {"start": v(-11.19, -13.2) * mm, "end": v(-12.5, -12.52) * mm});
            skLineSegment(sketch, "E329", {"start": v(-12.5, -12.52) * mm, "end": v(-14.41, -13.79) * mm});
            skLineSegment(sketch, "E330", {"start": v(-14.41, -13.79) * mm, "end": v(-15.42, -15.25) * mm});
            skLineSegment(sketch, "E331", {"start": v(-15.42, -15.25) * mm, "end": v(-16.44, -15.25) * mm});
            skLineSegment(sketch, "E332", {"start": v(-16.44, -15.25) * mm, "end": v(-16.44, -14.64) * mm});
            skLineSegment(sketch, "E333", {"start": v(-16.44, -14.64) * mm, "end": v(-17.4, -15.25) * mm});
            skLineSegment(sketch, "E334", {"start": v(-17.4, -15.25) * mm, "end": v(-19.28, -14.64) * mm});
            skLineSegment(sketch, "E335", {"start": v(-20.34, -14.64) * mm, "end": v(-20.8, -15.25) * mm});
            skLineSegment(sketch, "E336", {"start": v(-20.8, -15.25) * mm, "end": v(-21.6, -14.64) * mm});
            skLineSegment(sketch, "E337", {"start": v(-19.28, -14.64) * mm, "end": v(-20.34, -14.64) * mm});
            skLineSegment(sketch, "E338", {"start": v(-21.6, -14.64) * mm, "end": v(-23.22, -14.94) * mm});
            skPoint(sketch, "E338.endSnap0", {"position": v(-18.35, -14.94) * mm});
            skLineSegment(sketch, "E339", {"start": v(-23.22, -14.94) * mm, "end": v(-24.09, -14.94) * mm});
            skLineSegment(sketch, "E340", {"start": v(-24.09, -14.94) * mm, "end": v(-26.27, -14.94) * mm});
            skLineSegment(sketch, "E341", {"start": v(-26.27, -14.94) * mm, "end": v(-27.09, -15.25) * mm});
            skLineSegment(sketch, "E342", {"start": v(-27.09, -15.25) * mm, "end": v(-28.02, -14.94) * mm});
            skLineSegment(sketch, "E343", {"start": v(-28.02, -14.94) * mm, "end": v(-28.98, -15.74) * mm});
            skLineSegment(sketch, "E344", {"start": v(-30.98, -16.12) * mm, "end": v(-28.98, -15.74) * mm});
            skLineSegment(sketch, "E345", {"start": v(-30.98, -16.12) * mm, "end": v(-31.27, -14.64) * mm});
            skLineSegment(sketch, "E346", {"start": v(-31.27, -14.64) * mm, "end": v(-32.2, -14.34) * mm});
            skLineSegment(sketch, "E347", {"start": v(-32.2, -14.34) * mm, "end": v(-33.32, -14.34) * mm});
            skLineSegment(sketch, "E348", {"start": v(-33.32, -14.34) * mm, "end": v(-33.95, -14.34) * mm});
            skLineSegment(sketch, "E349", {"start": v(-33.95, -14.34) * mm, "end": v(-33.95, -12.52) * mm});
            skLineSegment(sketch, "E350", {"start": v(-33.95, -12.52) * mm, "end": v(-33.32, -10.6) * mm});
            skLineSegment(sketch, "E351", {"start": v(-33.32, -10.6) * mm, "end": v(-34.86, -9.9) * mm});
            skLineSegment(sketch, "E352", {"start": v(-34.86, -9.9) * mm, "end": v(-34.4, -8.5) * mm});
            skLineSegment(sketch, "E353", {"start": v(-34.4, -8.5) * mm, "end": v(-32.91, -7.26) * mm});
            skLineSegment(sketch, "E354", {"start": v(-32.91, -7.26) * mm, "end": v(-32.91, -5.77) * mm});
            skLineSegment(sketch, "E355", {"start": v(-32.91, -5.77) * mm, "end": v(-33.9, -3.89) * mm});
            skLineSegment(sketch, "E356", {"start": v(-33.9, -3.89) * mm, "end": v(-34.23, -3.49) * mm});
            skLineSegment(sketch, "E357", {"start": v(-34.23, -3.49) * mm, "end": v(-32.43, -2.67) * mm});
            skLineSegment(sketch, "E358", {"start": v(-32.43, -2.67) * mm, "end": v(-32.97, -1.47) * mm});
            skLineSegment(sketch, "E359", {"start": v(-32.97, -1.47) * mm, "end": v(-33.32, 0) * mm});
            skLineSegment(sketch, "E360", {"start": v(-33.32, 0) * mm, "end": v(-33.74, 0.5) * mm});
            skLineSegment(sketch, "E361", {"start": v(-33.74, 0.5) * mm, "end": v(-33.74, 2.52) * mm});
            skLineSegment(sketch, "E362", {"start": v(-33.74, 2.52) * mm, "end": v(-33.16, 4.3) * mm});
            skLineSegment(sketch, "E363", {"start": v(-33.16, 4.3) * mm, "end": v(-33.16, 5.15) * mm});
            skLineSegment(sketch, "E364", {"start": v(-33.16, 5.15) * mm, "end": v(-33.16, 7.32) * mm});
            skLineSegment(sketch, "E365", {"start": v(-33.16, 7.32) * mm, "end": v(-33.16, 8.42) * mm});
            skLineSegment(sketch, "E366", {"start": v(-33.16, 8.42) * mm, "end": v(-32.54, 8.42) * mm});
            skLineSegment(sketch, "E367", {"start": v(-32.54, 8.42) * mm, "end": v(-33.16, 9.17) * mm});
            skLineSegment(sketch, "E368", {"start": v(-33.16, 9.17) * mm, "end": v(-30.98, 9.17) * mm});
            skLineSegment(sketch, "E369", {"start": v(-30.98, 9.17) * mm, "end": v(-31.48, 10.84) * mm});
            skLineSegment(sketch, "E370", {"start": v(-31.48, 10.84) * mm, "end": v(-29.88, 10.84) * mm});
            skLineSegment(sketch, "E371", {"start": v(-29.88, 10.84) * mm, "end": v(-28.97, 10.99) * mm});
            skLineSegment(sketch, "E372", {"start": v(-28.97, 10.99) * mm, "end": v(-28.4, 10.8) * mm});
            skLineSegment(sketch, "E373", {"start": v(-28.4, 10.8) * mm, "end": v(-26.5, 10.8) * mm});
            skLineSegment(sketch, "E374", {"start": v(-26.5, 10.8) * mm, "end": v(-25.43, 10.46) * mm});
            skLineSegment(sketch, "E375", {"start": v(-25.43, 10.46) * mm, "end": v(-24.73, 10.63) * mm});
            skLineSegment(sketch, "E376", {"start": v(-24.73, 10.63) * mm, "end": v(-24.09, 10.42) * mm});
            skLineSegment(sketch, "E377", {"start": v(-24.09, 10.42) * mm, "end": v(-23.14, 10.42) * mm});
            skLineSegment(sketch, "E378", {"start": v(-23.14, 10.42) * mm, "end": v(-20.34, 10.42) * mm});
            skLineSegment(sketch, "E379", {"start": v(-19.28, 9.46) * mm, "end": v(-20.34, 10.42) * mm});
            skLineSegment(sketch, "E380", {"start": v(-19.28, 9.46) * mm, "end": v(-17.7, 10.76) * mm});
            skLineSegment(sketch, "E381", {"start": v(-17.7, 10.76) * mm, "end": v(-16.92, 10.76) * mm});
            skLineSegment(sketch, "E382", {"start": v(-16.92, 10.76) * mm, "end": v(-15.6, 11.3) * mm});
            skLineSegment(sketch, "E383", {"start": v(-15.6, 11.3) * mm, "end": v(-14.86, 10.42) * mm});
            skLineSegment(sketch, "E384", {"start": v(-14.86, 10.42) * mm, "end": v(-13.85, 11.26) * mm});
            skLineSegment(sketch, "E385", {"start": v(-13.85, 11.26) * mm, "end": v(-10.73, 9.46) * mm});
            skLineSegment(sketch, "E386", {"start": v(-10.73, 9.46) * mm, "end": v(-8.46, 11.16) * mm});
            skLineSegment(sketch, "E387", {"start": v(-8.46, 11.16) * mm, "end": v(-5.64, 9.46) * mm});
            skLineSegment(sketch, "E388", {"start": v(-5.64, 9.46) * mm, "end": v(-5.37, 9.46) * mm});
            skLineSegment(sketch, "E389", {"start": v(-5.37, 9.46) * mm, "end": v(-4.6, 10.1) * mm});
            skLineSegment(sketch, "E390", {"start": v(-4.6, 10.1) * mm, "end": v(-2.6, 9.46) * mm});
            skLineSegment(sketch, "E391", {"start": v(-2.6, 9.46) * mm, "end": v(-1.43, 10.42) * mm});
            skLineSegment(sketch, "E392", {"start": v(-1.43, 10.42) * mm, "end": v(-1.43, 10.94) * mm});
            skLineSegment(sketch, "E393", {"start": v(-1.43, 10.94) * mm, "end": v(-0.61, 10.65) * mm});
            skLineSegment(sketch, "E394", {"start": v(-0.61, 10.65) * mm, "end": v(1.87, 10.65) * mm});
            skLineSegment(sketch, "E395", {"start": v(1.87, 10.65) * mm, "end": v(1.87, 11.37) * mm});
            skLineSegment(sketch, "E396", {"start": v(1.87, 11.37) * mm, "end": v(2.84, 12.17) * mm});
            skLineSegment(sketch, "E397", {"start": v(2.84, 12.17) * mm, "end": v(2.84, 10.42) * mm});
            skLineSegment(sketch, "E398", {"start": v(2.84, 10.42) * mm, "end": v(3.86, 11.28) * mm});
            skLineSegment(sketch, "E399", {"start": v(3.86, 11.28) * mm, "end": v(5.28, 10.82) * mm});
            skLineSegment(sketch, "E400", {"start": v(5.28, 10.82) * mm, "end": v(7.26, 10.82) * mm});
            skLineSegment(sketch, "E401", {"start": v(7.26, 10.82) * mm, "end": v(8.46, 10.42) * mm});
            skLineSegment(sketch, "E402", {"start": v(8.46, 10.42) * mm, "end": v(9.88, 11.3) * mm});
            skLineSegment(sketch, "E403", {"start": v(9.88, 11.3) * mm, "end": v(10.24, 10.71) * mm});
            skLineSegment(sketch, "E404", {"start": v(10.24, 10.71) * mm, "end": v(11.7, 11.6) * mm});
            skLineSegment(sketch, "E405", {"start": v(11.7, 11.6) * mm, "end": v(12.68, 10.42) * mm});
            skLineSegment(sketch, "E406", {"start": v(12.68, 10.42) * mm, "end": v(13.23, 11.18) * mm});
            skLineSegment(sketch, "E407", {"start": v(13.23, 11.18) * mm, "end": v(15.55, 10.42) * mm});
            skLineSegment(sketch, "E408", {"start": v(15.55, 10.42) * mm, "end": v(16.58, 11.11) * mm});
            skLineSegment(sketch, "E409", {"start": v(16.58, 11.11) * mm, "end": v(17.15, 10.42) * mm});
            skLineSegment(sketch, "E410", {"start": v(17.15, 10.42) * mm, "end": v(17.33, 11) * mm});
            skLineSegment(sketch, "E411", {"start": v(17.33, 11) * mm, "end": v(19.08, 10.42) * mm});
            skLineSegment(sketch, "E412", {"start": v(19.08, 10.42) * mm, "end": v(19.94, 11.15) * mm});
            skLineSegment(sketch, "E413", {"start": v(19.94, 11.15) * mm, "end": v(20.94, 11.15) * mm});
            skLineSegment(sketch, "E414", {"start": v(20.94, 11.15) * mm, "end": v(22.45, 11.15) * mm});
            skLineSegment(sketch, "E415", {"start": v(22.45, 11.15) * mm, "end": v(25.69, 11.15) * mm});
            skLineSegment(sketch, "E416", {"start": v(25.69, 11.15) * mm, "end": v(26.96, 11.15) * mm});
            skLineSegment(sketch, "E417", {"start": v(26.96, 11.15) * mm, "end": v(28.46, 10.66) * mm});
            skLineSegment(sketch, "E418", {"start": v(28.46, 10.66) * mm, "end": v(29.04, 11.12) * mm});
            skLineSegment(sketch, "E419", {"start": v(29.04, 11.12) * mm, "end": v(30.31, 9.6) * mm});
            skLineSegment(sketch, "E420", {"start": v(30.31, 9.6) * mm, "end": v(32.67, 9.6) * mm});
            skLineSegment(sketch, "E421", {"start": v(32.67, 9.6) * mm, "end": v(32.47, 8.98) * mm});
            skLineSegment(sketch, "E422", {"start": v(32.47, 8.98) * mm, "end": v(32.47, 7.32) * mm});
            skLineSegment(sketch, "E423", {"start": v(32.47, 6.75) * mm, "end": v(32.47, 7.32) * mm});
            skLineSegment(sketch, "E424", {"start": v(32.47, 6.75) * mm, "end": v(32.47, 5.15) * mm});
            skLineSegment(sketch, "E425", {"start": v(32.47, 5.15) * mm, "end": v(33.02, 4.4) * mm});
            skLineSegment(sketch, "E426", {"start": v(33.02, 4.4) * mm, "end": v(32.47, 3.5) * mm});
            skLineSegment(sketch, "E427", {"start": v(32.47, 3.5) * mm, "end": v(32.81, 2.46) * mm});
            skLineSegment(sketch, "E428", {"start": v(32.81, 2.46) * mm, "end": v(32.38, 1.15) * mm});
            skLineSegment(sketch, "E429", {"start": v(32.38, 1.15) * mm, "end": v(32.97, -0.82) * mm});
            skLineSegment(sketch, "E430", {"start": v(32.97, -0.82) * mm, "end": v(31.96, -2.39) * mm});
            skLineSegment(sketch, "E431", {"start": v(31.96, -2.39) * mm, "end": v(32.47, -4.5) * mm});
            skLineSegment(sketch, "E432", {"start": v(32.47, -4.5) * mm, "end": v(31.82, -6.49) * mm});
            skLineSegment(sketch, "E433", {"start": v(31.82, -6.49) * mm, "end": v(32.47, -8.29) * mm});
            skLineSegment(sketch, "E434", {"start": v(32.47, -8.29) * mm, "end": v(32.47, -8.87) * mm});
            skLineSegment(sketch, "E435", {"start": v(32.47, -8.87) * mm, "end": v(32.97, -9.48) * mm});
            skLineSegment(sketch, "E436", {"start": v(32.97, -9.48) * mm, "end": v(32.1, -10.2) * mm});
            skLineSegment(sketch, "E437", {"start": v(32.1, -10.2) * mm, "end": v(32.1, -12.52) * mm});
            skLineSegment(sketch, "E438", {"start": v(32.1, -12.52) * mm, "end": v(31.06, -13.39) * mm});
            skLineSegment(sketch, "E439", {"start": v(31.06, -13.39) * mm, "end": v(29.18, -14.94) * mm});
            skLineSegment(sketch, "E440", {"start": v(29.18, -14.94) * mm, "end": v(28.82, -15.25) * mm});
            skLineSegment(sketch, "E441", {"start": v(28.82, -15.25) * mm, "end": v(26.6, -15.25) * mm});
            skLineSegment(sketch, "E442", {"start": v(26.6, -15.25) * mm, "end": v(25.51, -15.25) * mm});
            skLineSegment(sketch, "E443", {"start": v(25.51, -15.25) * mm, "end": v(23.68, -15.25) * mm});
            skLineSegment(sketch, "E444", {"start": v(23.68, -15.25) * mm, "end": v(22.74, -14.94) * mm});
            skLineSegment(sketch, "E445", {"start": v(22.74, -14.94) * mm, "end": v(22, -15.53) * mm});
            skLineSegment(sketch, "E446", {"start": v(22, -15.53) * mm, "end": v(20.2, -14.94) * mm});
            skLineSegment(sketch, "E447", {"start": v(20.2, -14.94) * mm, "end": v(19.7, -15.22) * mm});
            skLineSegment(sketch, "E448", {"start": v(19.7, -15.22) * mm, "end": v(18.33, -15.36) * mm});
            skLineSegment(sketch, "E449", {"start": v(18.33, -15.36) * mm, "end": v(17.73, -14.64) * mm});
            skLineSegment(sketch, "E450", {"start": v(17.73, -14.64) * mm, "end": v(19.04, -13.55) * mm});
            skLineSegment(sketch, "E451", {"start": v(19.04, -13.55) * mm, "end": v(18.19, -12.52) * mm});
            skLineSegment(sketch, "E452", {"start": v(18.19, -12.52) * mm, "end": v(17.79, -12.4) * mm});
            skLineSegment(sketch, "E453", {"start": v(17.79, -12.4) * mm, "end": v(20.54, -10.99) * mm});
            skLineSegment(sketch, "E454", {"start": v(20.54, -10.99) * mm, "end": v(20.94, -12.52) * mm});
            skLineSegment(sketch, "E455", {"start": v(20.94, -12.52) * mm, "end": v(21.8, -13.77) * mm});
            skLineSegment(sketch, "E456", {"start": v(21.8, -13.77) * mm, "end": v(22.86, -13.9) * mm});
            skLineSegment(sketch, "E457", {"start": v(22.86, -13.9) * mm, "end": v(24.04, -13.2) * mm});
            skLineSegment(sketch, "E458", {"start": v(24.04, -13.2) * mm, "end": v(24.47, -12) * mm});
            skLineSegment(sketch, "E459", {"start": v(24.47, -12) * mm, "end": v(25.18, -11.61) * mm});
            skLineSegment(sketch, "E460", {"start": v(25.18, -11.61) * mm, "end": v(26.6, -11.15) * mm});
            skLineSegment(sketch, "E461", {"start": v(26.6, -11.15) * mm, "end": v(28.71, -11.5) * mm});
            skLineSegment(sketch, "E462", {"start": v(28.71, -11.5) * mm, "end": v(28.4, -9.87) * mm});
            skLineSegment(sketch, "E463", {"start": v(28.4, -9.87) * mm, "end": v(28.46, -8.58) * mm});
            skLineSegment(sketch, "E464", {"start": v(28.46, -8.58) * mm, "end": v(28.6, -8.27) * mm});
            skLineSegment(sketch, "E465", {"start": v(28.6, -8.27) * mm, "end": v(28.88, -7.82) * mm});
            skLineSegment(sketch, "E466", {"start": v(28.88, -7.82) * mm, "end": v(28.76, -7.1) * mm});
            skLineSegment(sketch, "E467", {"start": v(28.76, -7.1) * mm, "end": v(28.52, -6.52) * mm});
            skLineSegment(sketch, "E468", {"start": v(28.52, -6.52) * mm, "end": v(28.72, -5.79) * mm});
            skLineSegment(sketch, "E469", {"start": v(28.72, -5.79) * mm, "end": v(28.91, -5.16) * mm});
            skLineSegment(sketch, "E470", {"start": v(29.14, -4.32) * mm, "end": v(28.9, -3.7) * mm});
            skLineSegment(sketch, "E471", {"start": v(28.9, -3.7) * mm, "end": v(28.61, -3.38) * mm});
            skLineSegment(sketch, "E472", {"start": v(28.61, -3.38) * mm, "end": v(28.9, -3.7) * mm});
            skLineSegment(sketch, "E473", {"start": v(28.91, -5.16) * mm, "end": v(29.14, -4.32) * mm});
            skLineSegment(sketch, "E474", {"start": v(28.61, -3.38) * mm, "end": v(28.91, -2.45) * mm});
            skLineSegment(sketch, "E475", {"start": v(28.91, -2.45) * mm, "end": v(29.04, -1.8) * mm});
            skLineSegment(sketch, "E476", {"start": v(29.04, -1.8) * mm, "end": v(30.09, -0.48) * mm});
            skLineSegment(sketch, "E477", {"start": v(30.09, -0.48) * mm, "end": v(29.25, 0.55) * mm});
            skLineSegment(sketch, "E478", {"start": v(29.25, 0.55) * mm, "end": v(29.25, 0.99) * mm});
            skLineSegment(sketch, "E479", {"start": v(29.25, 0.99) * mm, "end": v(28.61, 1.76) * mm});
            skLineSegment(sketch, "E480", {"start": v(28.61, 1.76) * mm, "end": v(29.43, 3.9) * mm});
            skLineSegment(sketch, "E481", {"start": v(29.43, 3.9) * mm, "end": v(29.13, 5.15) * mm});
            skLineSegment(sketch, "E482", {"start": v(29.13, 5.15) * mm, "end": v(29.99, 6.05) * mm});
            skLineSegment(sketch, "E483", {"start": v(29.99, 6.05) * mm, "end": v(28.65, 7.32) * mm});
            skLineSegment(sketch, "E484", {"start": v(28.65, 7.32) * mm, "end": v(27.83, 8.13) * mm});
            skLineSegment(sketch, "E485", {"start": v(27.83, 8.13) * mm, "end": v(27.35, 8.2) * mm});
            skLineSegment(sketch, "E486", {"start": v(27.35, 8.2) * mm, "end": v(26.66, 8.42) * mm});
            skLineSegment(sketch, "E487", {"start": v(26.66, 8.42) * mm, "end": v(25.4, 8.13) * mm});
            skLineSegment(sketch, "E488", {"start": v(25.4, 8.13) * mm, "end": v(24.37, 8.6) * mm});
            skLineSegment(sketch, "E489", {"start": v(24.37, 8.6) * mm, "end": v(23.48, 8.06) * mm});
            skLineSegment(sketch, "E490", {"start": v(23.48, 8.06) * mm, "end": v(22.4, 8.43) * mm});
            skLineSegment(sketch, "E491", {"start": v(22.4, 8.43) * mm, "end": v(21.93, 8.17) * mm});
            skLineSegment(sketch, "E492", {"start": v(21.93, 8.17) * mm, "end": v(20.46, 8.58) * mm});
            skLineSegment(sketch, "E493", {"start": v(20.46, 8.58) * mm, "end": v(19.8, 8.5) * mm});
            skLineSegment(sketch, "E494", {"start": v(19.8, 8.5) * mm, "end": v(19.04, 8.75) * mm});
            skLineSegment(sketch, "E495", {"start": v(19.04, 8.75) * mm, "end": v(18.3, 8.65) * mm});
            skLineSegment(sketch, "E496", {"start": v(18.3, 8.65) * mm, "end": v(17.47, 8.65) * mm});
            skLineSegment(sketch, "E497", {"start": v(17.47, 8.65) * mm, "end": v(16.12, 8.51) * mm});
            skLineSegment(sketch, "E498", {"start": v(16.12, 8.51) * mm, "end": v(15.17, 9.07) * mm});
            skLineSegment(sketch, "E499", {"start": v(15.17, 9.07) * mm, "end": v(14.26, 8.38) * mm});
            skLineSegment(sketch, "E500", {"start": v(14.26, 8.38) * mm, "end": v(12.74, 8.75) * mm});
            skLineSegment(sketch, "E501", {"start": v(12.74, 8.75) * mm, "end": v(11.52, 8.15) * mm});
            skLineSegment(sketch, "E502", {"start": v(11.52, 8.15) * mm, "end": v(9.62, 9.46) * mm});
            skLineSegment(sketch, "E503", {"start": v(9.62, 9.46) * mm, "end": v(8.98, 8.68) * mm});
            skLineSegment(sketch, "E504", {"start": v(8.98, 8.68) * mm, "end": v(7, 8.2) * mm});
            skLineSegment(sketch, "E505", {"start": v(7, 8.2) * mm, "end": v(5.69, 9.91) * mm});
            skLineSegment(sketch, "E506", {"start": v(5.69, 9.91) * mm, "end": v(4.38, 9.87) * mm});
            skLineSegment(sketch, "E507", {"start": v(4.38, 9.87) * mm, "end": v(2.63, 8.42) * mm});
            skLineSegment(sketch, "E508", {"start": v(2.63, 8.42) * mm, "end": v(0.51, 8.42) * mm});
            skLineSegment(sketch, "E509", {"start": v(0.51, 8.42) * mm, "end": v(-0.8, 7.58) * mm});
            skLineSegment(sketch, "E510", {"start": v(-0.8, 7.58) * mm, "end": v(-1.15, 8.23) * mm});
            skLineSegment(sketch, "E511", {"start": v(-1.15, 8.23) * mm, "end": v(-4.88, 7.32) * mm});
            skLineSegment(sketch, "E512", {"start": v(-4.88, 7.32) * mm, "end": v(-6.42, 7.74) * mm});
            skLineSegment(sketch, "E513", {"start": v(-6.42, 7.74) * mm, "end": v(-7.78, 8.14) * mm});
            skLineSegment(sketch, "E514", {"start": v(-7.78, 8.14) * mm, "end": v(-8.98, 8.42) * mm});
            skLineSegment(sketch, "E515", {"start": v(-8.98, 8.42) * mm, "end": v(-9.85, 8.42) * mm});
            skLineSegment(sketch, "E516", {"start": v(-9.85, 8.42) * mm, "end": v(-9.95, 8.1) * mm});
            skLineSegment(sketch, "E517", {"start": v(-9.95, 8.1) * mm, "end": v(-10.62, 7.32) * mm});
            skLineSegment(sketch, "E518", {"start": v(-10.62, 7.32) * mm, "end": v(-11.8, 8.03) * mm});
            skLineSegment(sketch, "E519", {"start": v(-11.8, 8.03) * mm, "end": v(-13.06, 7.72) * mm});
            skLineSegment(sketch, "E520", {"start": v(-13.06, 7.72) * mm, "end": v(-14.43, 8.27) * mm});
            skLineSegment(sketch, "E521", {"start": v(-14.43, 8.27) * mm, "end": v(-15.57, 7.32) * mm});
            skLineSegment(sketch, "E522", {"start": v(-15.57, 7.32) * mm, "end": v(-18.12, 7.8) * mm});
            skLineSegment(sketch, "E523", {"start": v(-18.12, 7.8) * mm, "end": v(-19.7, 7.35) * mm});
            skLineSegment(sketch, "E524", {"start": v(-19.7, 7.35) * mm, "end": v(-19.39, 8.07) * mm});
            skLineSegment(sketch, "E525", {"start": v(-19.39, 8.07) * mm, "end": v(-21.27, 7.78) * mm});
            skLineSegment(sketch, "E526", {"start": v(-21.27, 7.78) * mm, "end": v(-23.57, 7.6) * mm});
            skLineSegment(sketch, "E527", {"start": v(-24.02, 7.5) * mm, "end": v(-24.6, 8.2) * mm});
            skLineSegment(sketch, "E528", {"start": v(-24.6, 8.2) * mm, "end": v(-25.52, 7.2) * mm});
            skLineSegment(sketch, "E529", {"start": v(-25.52, 7.2) * mm, "end": v(-25.91, 7.91) * mm});
            skLineSegment(sketch, "E530", {"start": v(-25.91, 7.91) * mm, "end": v(-27.3, 7.18) * mm});
            skLineSegment(sketch, "E531", {"start": v(-27.3, 7.18) * mm, "end": v(-28.74, 7.8) * mm});
            skLineSegment(sketch, "E532", {"start": v(-28.74, 7.8) * mm, "end": v(-30.66, 6.43) * mm});
            skLineSegment(sketch, "E533", {"start": v(-30.66, 6.43) * mm, "end": v(-30.14, 5.06) * mm});
            skLineSegment(sketch, "E534", {"start": v(-30.14, 5.06) * mm, "end": v(-30.1, 4.18) * mm});
            skLineSegment(sketch, "E535", {"start": v(-30.1, 4.18) * mm, "end": v(-29.76, 2.79) * mm});
            skLineSegment(sketch, "E536", {"start": v(-29.76, 2.79) * mm, "end": v(-30.1, 0.6) * mm});
            skLineSegment(sketch, "E537", {"start": v(-30.1, 0.6) * mm, "end": v(-30.57, -0.97) * mm});
            skLineSegment(sketch, "E538", {"start": v(-30.57, -0.97) * mm, "end": v(-30.02, -1.63) * mm});
            skLineSegment(sketch, "E539", {"start": v(-30.02, -1.63) * mm, "end": v(-30.64, -2.64) * mm});
            skLineSegment(sketch, "E540", {"start": v(-30.64, -2.64) * mm, "end": v(-30.43, -3.54) * mm});
            skLineSegment(sketch, "E541", {"start": v(-30.43, -3.54) * mm, "end": v(-30.5, -5.6) * mm});
            skLineSegment(sketch, "E542", {"start": v(-30.5, -5.6) * mm, "end": v(-30.98, -5.6) * mm});
            skLineSegment(sketch, "E543", {"start": v(-30.98, -5.6) * mm, "end": v(-30.75, -6.76) * mm});
            skLineSegment(sketch, "E544", {"start": v(-30.75, -6.76) * mm, "end": v(-30.44, -7.67) * mm});
            skLineSegment(sketch, "E545", {"start": v(-30.1, -8.36) * mm, "end": v(-30.44, -7.67) * mm});
            skLineSegment(sketch, "E546", {"start": v(-30.1, -8.36) * mm, "end": v(-30.44, -9.4) * mm});
            skLineSegment(sketch, "E547", {"start": v(-30.44, -9.4) * mm, "end": v(-30.56, -10.96) * mm});
            skLineSegment(sketch, "E548", {"start": v(-30.56, -10.96) * mm, "end": v(-30.04, -11.96) * mm});
            skLineSegment(sketch, "E549", {"start": v(-30.04, -11.96) * mm, "end": v(-28.31, -12.52) * mm});
            skLineSegment(sketch, "E550", {"start": v(-28.31, -12.52) * mm, "end": v(-25.52, -11.85) * mm});
            skLineSegment(sketch, "E551", {"start": v(-25.52, -11.85) * mm, "end": v(-23.7, -12.38) * mm});
            skLineSegment(sketch, "E552", {"start": v(-23.7, -12.38) * mm, "end": v(-22.65, -11.76) * mm});
            skLineSegment(sketch, "E553", {"start": v(-22.65, -11.76) * mm, "end": v(-21.52, -12.67) * mm});
            skLineSegment(sketch, "E554", {"start": v(-21.52, -12.67) * mm, "end": v(-19.79, -12.25) * mm});
            skLineSegment(sketch, "E555", {"start": v(-19.79, -12.25) * mm, "end": v(-17.76, -12.52) * mm});
            skLineSegment(sketch, "E556", {"start": v(-17.76, -12.52) * mm, "end": v(-16.4, -12) * mm});
            skLineSegment(sketch, "E557", {"start": v(-16.4, -12) * mm, "end": v(-13.25, -11.24) * mm});
            skLineSegment(sketch, "E558", {"start": v(-13.25, -11.24) * mm, "end": v(-11.55, -12.27) * mm});
            skLineSegment(sketch, "E559", {"start": v(-11.55, -12.27) * mm, "end": v(-10.37, -13.19) * mm});
            skLineSegment(sketch, "E560", {"start": v(-10.37, -13.19) * mm, "end": v(-8.32, -11.62) * mm});
            skLineSegment(sketch, "E561", {"start": v(-8.32, -11.62) * mm, "end": v(-7.33, -11.53) * mm});
            skLineSegment(sketch, "E562", {"start": v(-7.33, -11.53) * mm, "end": v(-6.93, -12.19) * mm});
            skLineSegment(sketch, "E563", {"start": v(-6.93, -12.19) * mm, "end": v(-5.8, -12.18) * mm});
            skLineSegment(sketch, "E564", {"start": v(-5.8, -12.18) * mm, "end": v(-5.38, -11.52) * mm});
            skLineSegment(sketch, "E565", {"start": v(-5.38, -11.52) * mm, "end": v(-3.35, -11.74) * mm});
            skLineSegment(sketch, "E566", {"start": v(-3.35, -11.74) * mm, "end": v(-2.14, -11.58) * mm});
            skLineSegment(sketch, "E567", {"start": v(-2.14, -11.58) * mm, "end": v(-0.08, -11.64) * mm});
            skLineSegment(sketch, "E568", {"start": v(-0.08, -11.64) * mm, "end": v(0.16, -12.22) * mm});
            skLineSegment(sketch, "E569", {"start": v(0.16, -12.22) * mm, "end": v(2.86, -11.5) * mm});
            skLineSegment(sketch, "E570", {"start": v(2.86, -11.5) * mm, "end": v(4.06, -11.44) * mm});
            skLineSegment(sketch, "E571", {"start": v(4.06, -11.44) * mm, "end": v(5.5, -12.77) * mm});
            skLineSegment(sketch, "E572", {"start": v(5.5, -12.77) * mm, "end": v(9.6, -11.37) * mm});
            skLineSegment(sketch, "E573", {"start": v(9.6, -11.37) * mm, "end": v(10.36, -12.17) * mm});
            skLineSegment(sketch, "E574", {"start": v(10.36, -12.17) * mm, "end": v(13.5, -11.4) * mm});
            skLineSegment(sketch, "E575", {"start": v(13.5, -11.4) * mm, "end": v(16.23, -13.23) * mm});
            skLineSegment(sketch, "E576", {"start": v(15.54, -15.4) * mm, "end": v(14.96, -14.64) * mm});
            skLineSegment(sketch, "E577", {"start": v(14.96, -14.64) * mm, "end": v(14.05, -14.64) * mm});
            skLineSegment(sketch, "E578", {"start": v(-24.02, 7.5) * mm, "end": v(-23.57, 7.6) * mm});
            skSolve(sketch);
        }
        {
            var Q0;
            Q0=qCreatedBy(makeId("Top.planeOp"),FACE);
            var sketch = newSketch(context, id + "F4", { "sketchPlane" : qUnion([Q0])});
            skLineSegment(sketch, "E579", {"start": v(-22.5, 1.32) * mm, "end": v(-23.62, 2.81) * mm});
            skLineSegment(sketch, "E580", {"start": v(-23.62, 2.81) * mm, "end": v(-24.32, 2.81) * mm});
            skLineSegment(sketch, "E581", {"start": v(-24.32, 2.81) * mm, "end": v(-24.32, 3.16) * mm});
            skLineSegment(sketch, "E582", {"start": v(-24.32, 3.16) * mm, "end": v(-25.57, 3.16) * mm});
            skLineSegment(sketch, "E583", {"start": v(-25.57, 3.16) * mm, "end": v(-25.92, 2.74) * mm});
            skLineSegment(sketch, "E584", {"start": v(-25.92, 2.74) * mm, "end": v(-26.37, 4.38) * mm});
            skLineSegment(sketch, "E585", {"start": v(-26.37, 4.38) * mm, "end": v(-26.69, 5.25) * mm});
            skLineSegment(sketch, "E586", {"start": v(-26.69, 5.25) * mm, "end": v(-26.37, 5.36) * mm});
            skLineSegment(sketch, "E587", {"start": v(-26.37, 5.36) * mm, "end": v(-25.16, 5.36) * mm});
            skLineSegment(sketch, "E588", {"start": v(-25.16, 5.36) * mm, "end": v(-25.16, 5.67) * mm});
            skLineSegment(sketch, "E589", {"start": v(-25.16, 5.67) * mm, "end": v(-17.84, 5.67) * mm});
            skLineSegment(sketch, "E590", {"start": v(-17.84, 5.67) * mm, "end": v(-17.08, 5.36) * mm});
            skLineSegment(sketch, "E591", {"start": v(-17.08, 5.36) * mm, "end": v(-16.38, 5.04) * mm});
            skLineSegment(sketch, "E592", {"start": v(-16.38, 5.04) * mm, "end": v(-15.96, 5.04) * mm});
            skLineSegment(sketch, "E593", {"start": v(-15.96, 5.04) * mm, "end": v(-15.47, 4.76) * mm});
            skLineSegment(sketch, "E594", {"start": v(-15.47, 4.76) * mm, "end": v(-13.87, 3.79) * mm});
            skLineSegment(sketch, "E595", {"start": v(-13.87, 3.79) * mm, "end": v(-13.87, 3.37) * mm});
            skLineSegment(sketch, "E596", {"start": v(-13.87, 3.37) * mm, "end": v(-14.29, 3.37) * mm});
            skLineSegment(sketch, "E597", {"start": v(-14.29, 3.37) * mm, "end": v(-13.84, 2.43) * mm});
            skLineSegment(sketch, "E598", {"start": v(-13.84, 2.43) * mm, "end": v(-13.45, 2.43) * mm});
            skLineSegment(sketch, "E599", {"start": v(-13.45, 2.43) * mm, "end": v(-13.14, 0.93) * mm});
            skLineSegment(sketch, "E600", {"start": v(-13.14, 0.93) * mm, "end": v(-12.9, 0.62) * mm});
            skLineSegment(sketch, "E601", {"start": v(-12.9, 0.62) * mm, "end": v(-13.7, 0) * mm});
            skLineSegment(sketch, "E602", {"start": v(-13.7, 0) * mm, "end": v(-14.15, -0.74) * mm});
            skLineSegment(sketch, "E603", {"start": v(-15.61, -0.74) * mm, "end": v(-15.12, -1.37) * mm});
            skLineSegment(sketch, "E604", {"start": v(-15.12, -1.37) * mm, "end": v(-14.7, -1.75) * mm});
            skLineSegment(sketch, "E605", {"start": v(-14.7, -1.75) * mm, "end": v(-14.15, -1.75) * mm});
            skLineSegment(sketch, "E606", {"start": v(-14.15, -1.75) * mm, "end": v(-13.45, -2.55) * mm});
            skLineSegment(sketch, "E607", {"start": v(-13.45, -2.55) * mm, "end": v(-13.1, -2.55) * mm});
            skLineSegment(sketch, "E608", {"start": v(-13.1, -2.55) * mm, "end": v(-12.76, -3.32) * mm});
            skLineSegment(sketch, "E609", {"start": v(-12.76, -3.32) * mm, "end": v(-12.76, -5.13) * mm});
            skLineSegment(sketch, "E610", {"start": v(-12.76, -5.13) * mm, "end": v(-13.24, -5.9) * mm});
            skLineSegment(sketch, "E611", {"start": v(-13.24, -5.9) * mm, "end": v(-12.76, -6.52) * mm});
            skLineSegment(sketch, "E612", {"start": v(-12.76, -6.52) * mm, "end": v(-12.76, -7.22) * mm});
            skLineSegment(sketch, "E613", {"start": v(-12.76, -7.22) * mm, "end": v(-13.84, -7.98) * mm});
            skLineSegment(sketch, "E614", {"start": v(-13.84, -7.98) * mm, "end": v(-13.54, -8.4) * mm});
            skLineSegment(sketch, "E615", {"start": v(-13.54, -8.4) * mm, "end": v(-14.15, -8.84) * mm});
            skLineSegment(sketch, "E616", {"start": v(-14.15, -8.84) * mm, "end": v(-15.68, -8.54) * mm});
            skLineSegment(sketch, "E617", {"start": v(-15.68, -8.54) * mm, "end": v(-15.75, -8.9) * mm});
            skLineSegment(sketch, "E618", {"start": v(-15.75, -8.9) * mm, "end": v(-15.75, -9.45) * mm});
            skLineSegment(sketch, "E619", {"start": v(-15.75, -9.45) * mm, "end": v(-16.38, -9.45) * mm});
            skLineSegment(sketch, "E620", {"start": v(-16.38, -9.45) * mm, "end": v(-17.14, -9.8) * mm});
            skLineSegment(sketch, "E621", {"start": v(-17.14, -9.8) * mm, "end": v(-17.3, -9.45) * mm});
            skLineSegment(sketch, "E622", {"start": v(-17.3, -9.45) * mm, "end": v(-17.7, -9.45) * mm});
            skLineSegment(sketch, "E623", {"start": v(-17.7, -9.45) * mm, "end": v(-18.33, -8.54) * mm});
            skLineSegment(sketch, "E624", {"start": v(-18.33, -8.54) * mm, "end": v(-19, -8.54) * mm});
            skLineSegment(sketch, "E625", {"start": v(-19, -8.54) * mm, "end": v(-19.37, -9.7) * mm});
            skLineSegment(sketch, "E626", {"start": v(-19.37, -9.7) * mm, "end": v(-26, -9.7) * mm});
            skLineSegment(sketch, "E627", {"start": v(-26, -9.7) * mm, "end": v(-26, -8.86) * mm});
            skLineSegment(sketch, "E628", {"start": v(-26, -8.86) * mm, "end": v(-25.68, -8.26) * mm});
            skLineSegment(sketch, "E629", {"start": v(-25.68, -8.26) * mm, "end": v(-25.02, -8.26) * mm});
            skLineSegment(sketch, "E630", {"start": v(-25.02, -8.26) * mm, "end": v(-24.18, -7.98) * mm});
            skLineSegment(sketch, "E631", {"start": v(-24.18, -7.98) * mm, "end": v(-23.07, -7.43) * mm});
            skLineSegment(sketch, "E632", {"start": v(-23.07, -7.43) * mm, "end": v(-22.79, -7.43) * mm});
            skLineSegment(sketch, "E633", {"start": v(-22.79, -7.43) * mm, "end": v(-22.5, -6.63) * mm});
            skLineSegment(sketch, "E634", {"start": v(-22.5, -6.63) * mm, "end": v(-22.5, -5.93) * mm});
            skLineSegment(sketch, "E635", {"start": v(-22.5, -5.93) * mm, "end": v(-22.5, -5.37) * mm});
            skLineSegment(sketch, "E636", {"start": v(-22.5, -5.37) * mm, "end": v(-22.65, -4.85) * mm});
            skLineSegment(sketch, "E637", {"start": v(-22.65, -4.85) * mm, "end": v(-22.65, -3.87) * mm});
            skLineSegment(sketch, "E638", {"start": v(-22.65, -3.87) * mm, "end": v(-22.65, -3.32) * mm});
            skLineSegment(sketch, "E639", {"start": v(-22.65, -3.32) * mm, "end": v(-22.2, -3.32) * mm});
            skLineSegment(sketch, "E640", {"start": v(-22.2, -3.32) * mm, "end": v(-22.2, -4.22) * mm});
            skLineSegment(sketch, "E641", {"start": v(-22.2, -4.22) * mm, "end": v(-21.81, -5.06) * mm});
            skLineSegment(sketch, "E642", {"start": v(-21.81, -5.06) * mm, "end": v(-21.81, -6.07) * mm});
            skLineSegment(sketch, "E643", {"start": v(-21.81, -6.07) * mm, "end": v(-20.84, -7.78) * mm});
            skLineSegment(sketch, "E644", {"start": v(-20.84, -7.78) * mm, "end": v(-19.44, -8.26) * mm});
            skLineSegment(sketch, "E645", {"start": v(-19.44, -8.26) * mm, "end": v(-19, -7.78) * mm});
            skLineSegment(sketch, "E646", {"start": v(-19, -7.78) * mm, "end": v(-17.91, -7.78) * mm});
            skLineSegment(sketch, "E647", {"start": v(-17.91, -7.78) * mm, "end": v(-16.45, -7.78) * mm});
            skLineSegment(sketch, "E648", {"start": v(-16.45, -7.78) * mm, "end": v(-14.15, -6.8) * mm});
            skLineSegment(sketch, "E649", {"start": v(-14.15, -6.8) * mm, "end": v(-14.15, -4.43) * mm});
            skLineSegment(sketch, "E650", {"start": v(-14.15, -4.43) * mm, "end": v(-14.64, -3.94) * mm});
            skLineSegment(sketch, "E651", {"start": v(-14.64, -3.94) * mm, "end": v(-14.64, -3.67) * mm});
            skLineSegment(sketch, "E652", {"start": v(-14.64, -3.67) * mm, "end": v(-15.12, -3.32) * mm});
            skLineSegment(sketch, "E653", {"start": v(-15.12, -3.32) * mm, "end": v(-15.68, -2.97) * mm});
            skLineSegment(sketch, "E654", {"start": v(-15.68, -2.97) * mm, "end": v(-15.82, -2.48) * mm});
            skLineSegment(sketch, "E655", {"start": v(-15.82, -2.48) * mm, "end": v(-16.48, -2.2) * mm});
            skLineSegment(sketch, "E656", {"start": v(-16.48, -2.2) * mm, "end": v(-17.08, -2.2) * mm});
            skLineSegment(sketch, "E657", {"start": v(-17.08, -2.2) * mm, "end": v(-18.71, -2.2) * mm});
            skLineSegment(sketch, "E658", {"start": v(-18.71, -2.2) * mm, "end": v(-18.71, -2.62) * mm});
            skLineSegment(sketch, "E659", {"start": v(-18.71, -2.62) * mm, "end": v(-21.67, -2.62) * mm});
            skLineSegment(sketch, "E660", {"start": v(-21.67, -2.62) * mm, "end": v(-22.1, -2.2) * mm});
            skLineSegment(sketch, "E661", {"start": v(-22.1, -2.2) * mm, "end": v(-22.5, -2.06) * mm});
            skLineSegment(sketch, "E662", {"start": v(-22.5, -2.06) * mm, "end": v(-23, -1.58) * mm});
            skLineSegment(sketch, "E663", {"start": v(-23, -1.58) * mm, "end": v(-23, -0.74) * mm});
            skLineSegment(sketch, "E664", {"start": v(-23, -0.74) * mm, "end": v(-23, -0.32) * mm});
            skLineSegment(sketch, "E665", {"start": v(-23, -0.32) * mm, "end": v(-22.79, 0.51) * mm});
            skLineSegment(sketch, "E666", {"start": v(-22.79, 0.51) * mm, "end": v(-22.5, 1.32) * mm});
            skLineSegment(sketch, "E667", {"start": v(-21.67, 1.32) * mm, "end": v(-19.93, 1.7) * mm});
            skLineSegment(sketch, "E668", {"start": v(-19.93, 1.7) * mm, "end": v(-19.93, 2.88) * mm});
            skLineSegment(sketch, "E669", {"start": v(-19.93, 2.88) * mm, "end": v(-18.75, 2.88) * mm});
            skLineSegment(sketch, "E670", {"start": v(-18.75, 2.88) * mm, "end": v(-17.84, 2.88) * mm});
            skLineSegment(sketch, "E671", {"start": v(-17.84, 2.88) * mm, "end": v(-16.48, 2.43) * mm});
            skLineSegment(sketch, "E672", {"start": v(-16.48, 2.43) * mm, "end": v(-15.12, 0.62) * mm});
            skLineSegment(sketch, "E673", {"start": v(-15.12, 0.62) * mm, "end": v(-16.48, -0.4) * mm});
            skLineSegment(sketch, "E674", {"start": v(-16.48, -0.4) * mm, "end": v(-17.88, -1.02) * mm});
            skLineSegment(sketch, "E675", {"start": v(-17.88, -1.02) * mm, "end": v(-18.19, -1.37) * mm});
            skLineSegment(sketch, "E676", {"start": v(-18.19, -1.37) * mm, "end": v(-18.89, -0.74) * mm});
            skLineSegment(sketch, "E677", {"start": v(-18.89, -0.74) * mm, "end": v(-20.38, -0.74) * mm});
            skLineSegment(sketch, "E678", {"start": v(-20.38, -0.74) * mm, "end": v(-21.32, 0) * mm});
            skLineSegment(sketch, "E679", {"start": v(-21.32, 0) * mm, "end": v(-21.32, 0.93) * mm});
            skLineSegment(sketch, "E680", {"start": v(-21.32, 0.93) * mm, "end": v(-21.67, 1.32) * mm});
            skLineSegment(sketch, "E681", {"start": v(-15.61, -0.74) * mm, "end": v(-14.15, -0.74) * mm});
            skLineSegment(sketch, "E682", {"start": v(-4.33, 0.83) * mm, "end": v(-2.97, 0.83) * mm});
            skLineSegment(sketch, "E683", {"start": v(-2.97, 0.83) * mm, "end": v(-2.9, 1.35) * mm});
            skLineSegment(sketch, "E684", {"start": v(-2.9, 1.35) * mm, "end": v(-3.46, 1.73) * mm});
            skLineSegment(sketch, "E685", {"start": v(-3.46, 1.73) * mm, "end": v(-3.3, 2.21) * mm});
            skLineSegment(sketch, "E686", {"start": v(-3.3, 2.21) * mm, "end": v(-3.04, 3.2) * mm});
            skLineSegment(sketch, "E687", {"start": v(-3.04, 3.2) * mm, "end": v(-3.35, 3.61) * mm});
            skLineSegment(sketch, "E688", {"start": v(-3.35, 3.61) * mm, "end": v(-4.08, 4.38) * mm});
            skLineSegment(sketch, "E689", {"start": v(-4.08, 4.38) * mm, "end": v(-2, 4.97) * mm});
            skLineSegment(sketch, "E690", {"start": v(-2, 4.97) * mm, "end": v(-2.62, 5.5) * mm});
            skLineSegment(sketch, "E691", {"start": v(-2.62, 5.5) * mm, "end": v(-3.7, 5.86) * mm});
            skLineSegment(sketch, "E692", {"start": v(-3.7, 5.86) * mm, "end": v(-5.2, 6.35) * mm});
            skLineSegment(sketch, "E693", {"start": v(-5.2, 6.35) * mm, "end": v(-5.93, 6.6) * mm});
            skLineSegment(sketch, "E694", {"start": v(-5.93, 6.6) * mm, "end": v(-6.87, 6.68) * mm});
            skLineSegment(sketch, "E695", {"start": v(-6.87, 6.68) * mm, "end": v(-7.98, 6.6) * mm});
            skLineSegment(sketch, "E696", {"start": v(-7.98, 6.6) * mm, "end": v(-9.24, 6.26) * mm});
            skLineSegment(sketch, "E697", {"start": v(-9.24, 6.26) * mm, "end": v(-10.21, 5.77) * mm});
            skLineSegment(sketch, "E698", {"start": v(-10.21, 5.77) * mm, "end": v(-10.35, 5.25) * mm});
            skLineSegment(sketch, "E699", {"start": v(-10.35, 5.25) * mm, "end": v(-10.35, 4.66) * mm});
            skLineSegment(sketch, "E700", {"start": v(-10.35, 4.66) * mm, "end": v(-10.07, 4.38) * mm});
            skLineSegment(sketch, "E701", {"start": v(-10.07, 4.38) * mm, "end": v(-9.66, 4.1) * mm});
            skLineSegment(sketch, "E702", {"start": v(-9.66, 4.1) * mm, "end": v(-9.13, 3.93) * mm});
            skLineSegment(sketch, "E703", {"start": v(-9.13, 3.93) * mm, "end": v(-8.12, 4.24) * mm});
            skLineSegment(sketch, "E704", {"start": v(-8.12, 4.24) * mm, "end": v(-7.7, 4.38) * mm});
            skLineSegment(sketch, "E705", {"start": v(-7.7, 4.38) * mm, "end": v(-7.7, 1.87) * mm});
            skLineSegment(sketch, "E706", {"start": v(-7.7, 1.87) * mm, "end": v(-7.7, 0.98) * mm});
            skLineSegment(sketch, "E707", {"start": v(-7.7, 0.98) * mm, "end": v(-7.48, 0.55) * mm});
            skLineSegment(sketch, "E708", {"start": v(-7.48, 0.55) * mm, "end": v(-7.49, 0.06) * mm});
            skLineSegment(sketch, "E709", {"start": v(-7.49, 0.06) * mm, "end": v(-7.24, -0.27) * mm});
            skLineSegment(sketch, "E710", {"start": v(-7.24, -0.27) * mm, "end": v(-7, -0.68) * mm});
            skLineSegment(sketch, "E711", {"start": v(-7, -0.68) * mm, "end": v(-7.72, -1.5) * mm});
            skLineSegment(sketch, "E712", {"start": v(-7.72, -1.5) * mm, "end": v(-7.81, -1.77) * mm});
            skLineSegment(sketch, "E713", {"start": v(-7.81, -1.77) * mm, "end": v(-7.72, -2.05) * mm});
            skLineSegment(sketch, "E714", {"start": v(-7.72, -2.05) * mm, "end": v(-7.72, -2.32) * mm});
            skLineSegment(sketch, "E715", {"start": v(-7.72, -2.32) * mm, "end": v(-7.49, -2.46) * mm});
            skLineSegment(sketch, "E716", {"start": v(-7.49, -2.46) * mm, "end": v(-7.49, -7.3) * mm});
            skLineSegment(sketch, "E717", {"start": v(-7.49, -7.3) * mm, "end": v(-8.12, -7.78) * mm});
            skLineSegment(sketch, "E718", {"start": v(-8.12, -7.78) * mm, "end": v(-8, -8) * mm});
            skLineSegment(sketch, "E719", {"start": v(-8, -8) * mm, "end": v(-8.79, -8.35) * mm});
            skLineSegment(sketch, "E720", {"start": v(-8.79, -8.35) * mm, "end": v(-9.13, -8.78) * mm});
            skLineSegment(sketch, "E721", {"start": v(-9.13, -8.78) * mm, "end": v(-9.65, -9.21) * mm});
            skLineSegment(sketch, "E722", {"start": v(-9.65, -9.21) * mm, "end": v(-9.3, -9.73) * mm});
            skLineSegment(sketch, "E723", {"start": v(-9.3, -9.73) * mm, "end": v(-8.44, -10.34) * mm});
            skLineSegment(sketch, "E724", {"start": v(-8.44, -10.34) * mm, "end": v(-7.49, -10.2) * mm});
            skLineSegment(sketch, "E725", {"start": v(-7.49, -10.2) * mm, "end": v(-6.97, -9.99) * mm});
            skLineSegment(sketch, "E726", {"start": v(-6.97, -9.99) * mm, "end": v(-5.67, -9.73) * mm});
            skLineSegment(sketch, "E727", {"start": v(-5.67, -9.73) * mm, "end": v(-5.15, -9.56) * mm});
            skLineSegment(sketch, "E728", {"start": v(-5.15, -9.56) * mm, "end": v(-4.46, -9.38) * mm});
            skLineSegment(sketch, "E729", {"start": v(-4.46, -9.38) * mm, "end": v(-4.38, -8.86) * mm});
            skLineSegment(sketch, "E730", {"start": v(-4.38, -8.86) * mm, "end": v(-4.76, -8.17) * mm});
            skLineSegment(sketch, "E731", {"start": v(-4.76, -8.17) * mm, "end": v(-5.15, -7.78) * mm});
            skLineSegment(sketch, "E732", {"start": v(-5.15, -7.78) * mm, "end": v(-5.15, -5.92) * mm});
            skLineSegment(sketch, "E733", {"start": v(-5.15, -5.92) * mm, "end": v(-5.33, -5.58) * mm});
            skLineSegment(sketch, "E734", {"start": v(-5.33, -5.58) * mm, "end": v(-5.5, -4.97) * mm});
            skLineSegment(sketch, "E735", {"start": v(-5.5, -4.97) * mm, "end": v(-6.02, -4.84) * mm});
            skLineSegment(sketch, "E736", {"start": v(-6.02, -4.84) * mm, "end": v(-4.76, -4.1) * mm});
            skLineSegment(sketch, "E737", {"start": v(-4.76, -4.1) * mm, "end": v(-5.15, -3.41) * mm});
            skLineSegment(sketch, "E738", {"start": v(-5.15, -3.41) * mm, "end": v(-5.5, -2.98) * mm});
            skLineSegment(sketch, "E739", {"start": v(-5.5, -2.98) * mm, "end": v(-5.85, -2.55) * mm});
            skLineSegment(sketch, "E740", {"start": v(-5.85, -2.55) * mm, "end": v(-5.59, -1.9) * mm});
            skLineSegment(sketch, "E741", {"start": v(-5.59, -1.9) * mm, "end": v(-5.15, -1.42) * mm});
            skLineSegment(sketch, "E742", {"start": v(-5.15, -1.42) * mm, "end": v(-5.98, -0.68) * mm});
            skLineSegment(sketch, "E743", {"start": v(-5.98, -0.68) * mm, "end": v(-5.93, 0.7) * mm});
            skLineSegment(sketch, "E744", {"start": v(-5.93, 0.7) * mm, "end": v(-5.85, 1.34) * mm});
            skLineSegment(sketch, "E745", {"start": v(-5.85, 1.34) * mm, "end": v(-6.28, 1.69) * mm});
            skLineSegment(sketch, "E746", {"start": v(-6.28, 1.69) * mm, "end": v(-6.37, 1.95) * mm});
            skLineSegment(sketch, "E747", {"start": v(-6.37, 1.95) * mm, "end": v(-5.76, 2.25) * mm});
            skLineSegment(sketch, "E748", {"start": v(-5.76, 2.25) * mm, "end": v(-5.15, 2.04) * mm});
            skLineSegment(sketch, "E749", {"start": v(-5.15, 2.04) * mm, "end": v(-4.46, 1.52) * mm});
            skLineSegment(sketch, "E750", {"start": v(-4.46, 1.52) * mm, "end": v(-4.33, 0.83) * mm});
            skLineSegment(sketch, "E751", {"start": v(-3.93, -0.74) * mm, "end": v(-3.5, -0.49) * mm});
            skLineSegment(sketch, "E752", {"start": v(-3.5, -0.49) * mm, "end": v(-3.17, -0.78) * mm});
            skLineSegment(sketch, "E753", {"start": v(-3.17, -0.78) * mm, "end": v(-2.99, -1.23) * mm});
            skLineSegment(sketch, "E754", {"start": v(-2.99, -1.23) * mm, "end": v(-2.4, -1.14) * mm});
            skLineSegment(sketch, "E755", {"start": v(-2.4, -1.14) * mm, "end": v(-2.39, -1.96) * mm});
            skLineSegment(sketch, "E756", {"start": v(-2.39, -1.96) * mm, "end": v(-2.59, -1.96) * mm});
            skLineSegment(sketch, "E757", {"start": v(-2.59, -1.96) * mm, "end": v(-2.6, -2.45) * mm});
            skLineSegment(sketch, "E758", {"start": v(-2.6, -2.45) * mm, "end": v(-2.19, -2.82) * mm});
            skLineSegment(sketch, "E759", {"start": v(-2.19, -2.82) * mm, "end": v(-2, -2.82) * mm});
            skLineSegment(sketch, "E760", {"start": v(-2, -2.82) * mm, "end": v(-1.53, -3.32) * mm});
            skLineSegment(sketch, "E761", {"start": v(-1.53, -3.32) * mm, "end": v(-2.4, -4.34) * mm});
            skLineSegment(sketch, "E762", {"start": v(-2.4, -4.34) * mm, "end": v(-2.04, -4.45) * mm});
            skLineSegment(sketch, "E763", {"start": v(-2.04, -4.45) * mm, "end": v(-1.75, -4.78) * mm});
            skLineSegment(sketch, "E764", {"start": v(-1.75, -4.78) * mm, "end": v(-1.64, -5.25) * mm});
            skLineSegment(sketch, "E765", {"start": v(-1.64, -5.25) * mm, "end": v(-1.53, -5.62) * mm});
            skLineSegment(sketch, "E766", {"start": v(-1.53, -5.62) * mm, "end": v(-1.2, -5.8) * mm});
            skLineSegment(sketch, "E767", {"start": v(-1.2, -5.8) * mm, "end": v(-0.71, -5.9) * mm});
            skLineSegment(sketch, "E768", {"start": v(-0.71, -5.9) * mm, "end": v(-0.37, -5.83) * mm});
            skLineSegment(sketch, "E769", {"start": v(-0.37, -5.83) * mm, "end": v(0.01, -5.72) * mm});
            skLineSegment(sketch, "E770", {"start": v(0.01, -5.72) * mm, "end": v(0.29, -5.58) * mm});
            skLineSegment(sketch, "E771", {"start": v(0.29, -5.58) * mm, "end": v(0.61, -5.6) * mm});
            skLineSegment(sketch, "E772", {"start": v(0.61, -5.6) * mm, "end": v(1.05, -5.6) * mm});
            skLineSegment(sketch, "E773", {"start": v(1.05, -5.6) * mm, "end": v(1.12, -5.76) * mm});
            skLineSegment(sketch, "E774", {"start": v(1.12, -5.76) * mm, "end": v(0.5, -6.16) * mm});
            skLineSegment(sketch, "E775", {"start": v(0.5, -6.16) * mm, "end": v(0.43, -7.87) * mm});
            skLineSegment(sketch, "E776", {"start": v(0.43, -7.87) * mm, "end": v(0.21, -7.87) * mm});
            skLineSegment(sketch, "E777", {"start": v(0.21, -7.87) * mm, "end": v(0.29, -9.58) * mm});
            skLineSegment(sketch, "E778", {"start": v(0.29, -9.58) * mm, "end": v(-0.13, -9.73) * mm});
            skLineSegment(sketch, "E779", {"start": v(-0.13, -9.73) * mm, "end": v(-0.37, -9.76) * mm});
            skLineSegment(sketch, "E780", {"start": v(-0.37, -9.76) * mm, "end": v(-0.88, -9.62) * mm});
            skLineSegment(sketch, "E781", {"start": v(-0.88, -9.62) * mm, "end": v(-1.31, -9.4) * mm});
            skLineSegment(sketch, "E782", {"start": v(-1.31, -9.4) * mm, "end": v(-1.6, -9.25) * mm});
            skLineSegment(sketch, "E783", {"start": v(-1.6, -9.25) * mm, "end": v(-2.04, -9.1) * mm});
            skLineSegment(sketch, "E784", {"start": v(-2.04, -9.1) * mm, "end": v(-2.46, -8.74) * mm});
            skLineSegment(sketch, "E785", {"start": v(-2.46, -8.74) * mm, "end": v(-2.68, -8.74) * mm});
            skLineSegment(sketch, "E786", {"start": v(-2.68, -8.74) * mm, "end": v(-2.26, -8.49) * mm});
            skLineSegment(sketch, "E787", {"start": v(-2.26, -8.49) * mm, "end": v(-1.9, -8.16) * mm});
            skLineSegment(sketch, "E788", {"start": v(-1.9, -8.16) * mm, "end": v(-1.66, -7.94) * mm});
            skLineSegment(sketch, "E789", {"start": v(-1.66, -7.94) * mm, "end": v(-1.68, -7.14) * mm});
            skLineSegment(sketch, "E790", {"start": v(-1.68, -7.14) * mm, "end": v(-2.26, -6.3) * mm});
            skLineSegment(sketch, "E791", {"start": v(-2.26, -6.3) * mm, "end": v(-2.7, -5.69) * mm});
            skLineSegment(sketch, "E792", {"start": v(-2.7, -5.69) * mm, "end": v(-3.31, -5.1) * mm});
            skLineSegment(sketch, "E793", {"start": v(-3.31, -5.1) * mm, "end": v(-3.42, -4.7) * mm});
            skLineSegment(sketch, "E794", {"start": v(-3.42, -4.7) * mm, "end": v(-3.53, -4.29) * mm});
            skLineSegment(sketch, "E795", {"start": v(-3.53, -4.29) * mm, "end": v(-2.7, -3.32) * mm});
            skLineSegment(sketch, "E796", {"start": v(-2.7, -3.32) * mm, "end": v(-2.99, -3.1) * mm});
            skLineSegment(sketch, "E797", {"start": v(-2.99, -3.1) * mm, "end": v(-3.35, -3.1) * mm});
            skLineSegment(sketch, "E798", {"start": v(-3.35, -3.1) * mm, "end": v(-3.57, -3) * mm});
            skLineSegment(sketch, "E799", {"start": v(-3.57, -3) * mm, "end": v(-3.97, -2.9) * mm});
            skLineSegment(sketch, "E800", {"start": v(-3.97, -2.9) * mm, "end": v(-4, -1.89) * mm});
            skLineSegment(sketch, "E801", {"start": v(-4, -1.89) * mm, "end": v(-3.75, -1.9) * mm});
            skLineSegment(sketch, "E802", {"start": v(-3.75, -1.9) * mm, "end": v(-3.93, -0.74) * mm});
            skLineSegment(sketch, "E803", {"start": v(-3.93, -8.74) * mm, "end": v(-3.87, -8.54) * mm});
            skLineSegment(sketch, "E804", {"start": v(-3.87, -8.54) * mm, "end": v(-3.55, -8.5) * mm});
            skLineSegment(sketch, "E805", {"start": v(-3.55, -8.5) * mm, "end": v(-3.2, -8.63) * mm});
            skLineSegment(sketch, "E806", {"start": v(-3.2, -8.63) * mm, "end": v(-2.97, -8.74) * mm});
            skLineSegment(sketch, "E807", {"start": v(-2.97, -8.74) * mm, "end": v(-3.06, -8.82) * mm});
            skLineSegment(sketch, "E808", {"start": v(-3.06, -8.82) * mm, "end": v(-3.35, -9.1) * mm});
            skLineSegment(sketch, "E809", {"start": v(-3.35, -9.1) * mm, "end": v(-3.79, -9.07) * mm});
            skLineSegment(sketch, "E810", {"start": v(-3.79, -9.07) * mm, "end": v(-3.93, -8.82) * mm});
            skLineSegment(sketch, "E811", {"start": v(3.9, 1.32) * mm, "end": v(3.4, 0.83) * mm});
            skLineSegment(sketch, "E812", {"start": v(3.4, 0.83) * mm, "end": v(3.37, 0.07) * mm});
            skLineSegment(sketch, "E813", {"start": v(3.37, 0.07) * mm, "end": v(3.03, -0.95) * mm});
            skLineSegment(sketch, "E814", {"start": v(3.03, -0.95) * mm, "end": v(2.92, -1.2) * mm});
            skLineSegment(sketch, "E815", {"start": v(2.92, -1.2) * mm, "end": v(2.65, -1.28) * mm});
            skLineSegment(sketch, "E816", {"start": v(2.65, -1.28) * mm, "end": v(2.13, -2.28) * mm});
            skLineSegment(sketch, "E817", {"start": v(2.13, -2.28) * mm, "end": v(2.02, -2.5) * mm});
            skLineSegment(sketch, "E818", {"start": v(2.02, -2.5) * mm, "end": v(1.93, -2.87) * mm});
            skLineSegment(sketch, "E819", {"start": v(1.93, -2.87) * mm, "end": v(1.75, -3.45) * mm});
            skLineSegment(sketch, "E820", {"start": v(1.75, -3.45) * mm, "end": v(1.56, -3.77) * mm});
            skLineSegment(sketch, "E821", {"start": v(1.56, -3.77) * mm, "end": v(1.36, -4.17) * mm});
            skLineSegment(sketch, "E822", {"start": v(1.36, -4.17) * mm, "end": v(1.18, -4.36) * mm});
            skLineSegment(sketch, "E823", {"start": v(1.18, -4.36) * mm, "end": v(0.9, -4.47) * mm});
            skLineSegment(sketch, "E824", {"start": v(0.9, -4.47) * mm, "end": v(0.86, -4.22) * mm});
            skLineSegment(sketch, "E825", {"start": v(0.86, -4.22) * mm, "end": v(0.64, -4.04) * mm});
            skLineSegment(sketch, "E826", {"start": v(0.64, -4.04) * mm, "end": v(0.64, -3.84) * mm});
            skLineSegment(sketch, "E827", {"start": v(0.64, -3.84) * mm, "end": v(0.73, -3.5) * mm});
            skLineSegment(sketch, "E828", {"start": v(0.73, -3.5) * mm, "end": v(1.05, -3) * mm});
            skLineSegment(sketch, "E829", {"start": v(1.05, -3) * mm, "end": v(1.18, -2.84) * mm});
            skLineSegment(sketch, "E830", {"start": v(1.18, -2.84) * mm, "end": v(1.32, -2.5) * mm});
            skLineSegment(sketch, "E831", {"start": v(1.32, -2.5) * mm, "end": v(1.45, -2.28) * mm});
            skLineSegment(sketch, "E832", {"start": v(1.45, -2.28) * mm, "end": v(1.56, -1.85) * mm});
            skLineSegment(sketch, "E833", {"start": v(1.56, -1.85) * mm, "end": v(1.77, -0.88) * mm});
            skLineSegment(sketch, "E834", {"start": v(1.77, -0.88) * mm, "end": v(1.81, -0.7) * mm});
            skLineSegment(sketch, "E835", {"start": v(1.81, -0.7) * mm, "end": v(2.08, -0.47) * mm});
            skLineSegment(sketch, "E836", {"start": v(2.08, -0.47) * mm, "end": v(2.26, -0.3) * mm});
            skLineSegment(sketch, "E837", {"start": v(2.26, -0.3) * mm, "end": v(2.29, -0.04) * mm});
            skLineSegment(sketch, "E838", {"start": v(2.29, -0.04) * mm, "end": v(2, 0.3) * mm});
            skLineSegment(sketch, "E839", {"start": v(2, 0.3) * mm, "end": v(1.63, 0.57) * mm});
            skLineSegment(sketch, "E840", {"start": v(1.63, 0.57) * mm, "end": v(1.59, 1.02) * mm});
            skLineSegment(sketch, "E841", {"start": v(1.59, 1.02) * mm, "end": v(2.08, 1.38) * mm});
            skLineSegment(sketch, "E842", {"start": v(2.08, 1.38) * mm, "end": v(2.67, 1.79) * mm});
            skLineSegment(sketch, "E843", {"start": v(2.67, 1.79) * mm, "end": v(2.8, 1.86) * mm});
            skLineSegment(sketch, "E844", {"start": v(2.8, 1.86) * mm, "end": v(2.9, 2.83) * mm});
            skLineSegment(sketch, "E845", {"start": v(2.9, 2.83) * mm, "end": v(3.21, 3.05) * mm});
            skLineSegment(sketch, "E846", {"start": v(3.21, 3.05) * mm, "end": v(3.26, 3.64) * mm});
            skLineSegment(sketch, "E847", {"start": v(3.26, 3.64) * mm, "end": v(2.9, 3.66) * mm});
            skLineSegment(sketch, "E848", {"start": v(2.9, 3.66) * mm, "end": v(2.9, 3.96) * mm});
            skLineSegment(sketch, "E849", {"start": v(2.9, 3.96) * mm, "end": v(3.44, 4.45) * mm});
            skLineSegment(sketch, "E850", {"start": v(3.44, 4.45) * mm, "end": v(3.5, 5.8) * mm});
            skLineSegment(sketch, "E851", {"start": v(3.5, 5.8) * mm, "end": v(3.57, 6.1) * mm});
            skLineSegment(sketch, "E852", {"start": v(3.57, 6.1) * mm, "end": v(3.94, 6.3) * mm});
            skLineSegment(sketch, "E853", {"start": v(3.94, 6.3) * mm, "end": v(5.04, 6.35) * mm});
            skLineSegment(sketch, "E854", {"start": v(5.04, 6.35) * mm, "end": v(5.47, 6.03) * mm});
            skLineSegment(sketch, "E855", {"start": v(5.47, 6.03) * mm, "end": v(5.74, 6.35) * mm});
            skLineSegment(sketch, "E856", {"start": v(5.74, 6.35) * mm, "end": v(6.06, 6.48) * mm});
            skLineSegment(sketch, "E857", {"start": v(6.06, 6.48) * mm, "end": v(6.38, 6.44) * mm});
            skLineSegment(sketch, "E858", {"start": v(6.38, 6.44) * mm, "end": v(6.74, 6.35) * mm});
            skLineSegment(sketch, "E859", {"start": v(6.74, 6.35) * mm, "end": v(7.05, 6.26) * mm});
            skLineSegment(sketch, "E860", {"start": v(7.05, 6.26) * mm, "end": v(7.19, 6.17) * mm});
            skLineSegment(sketch, "E861", {"start": v(7.19, 6.17) * mm, "end": v(7.14, 5.85) * mm});
            skLineSegment(sketch, "E862", {"start": v(7.14, 5.85) * mm, "end": v(7.46, 5.4) * mm});
            skLineSegment(sketch, "E863", {"start": v(7.46, 5.4) * mm, "end": v(7.69, 5.13) * mm});
            skLineSegment(sketch, "E864", {"start": v(7.69, 5.13) * mm, "end": v(7.87, 4.95) * mm});
            skLineSegment(sketch, "E865", {"start": v(7.87, 4.95) * mm, "end": v(7.91, 4.72) * mm});
            skLineSegment(sketch, "E866", {"start": v(7.91, 4.72) * mm, "end": v(7.46, 4.66) * mm});
            skLineSegment(sketch, "E867", {"start": v(7.46, 4.66) * mm, "end": v(6.92, 4.32) * mm});
            skLineSegment(sketch, "E868", {"start": v(6.92, 4.32) * mm, "end": v(6.56, 4.23) * mm});
            skLineSegment(sketch, "E869", {"start": v(6.56, 4.23) * mm, "end": v(6.15, 3.87) * mm});
            skLineSegment(sketch, "E870", {"start": v(6.15, 3.87) * mm, "end": v(6.01, 3.57) * mm});
            skLineSegment(sketch, "E871", {"start": v(6.01, 3.57) * mm, "end": v(5.83, 3.1) * mm});
            skLineSegment(sketch, "E872", {"start": v(5.83, 3.1) * mm, "end": v(5.83, 0) * mm});
            skLineSegment(sketch, "E873", {"start": v(5.83, 0) * mm, "end": v(5.65, -0.22) * mm});
            skLineSegment(sketch, "E874", {"start": v(5.65, -0.22) * mm, "end": v(5.16, -0.56) * mm});
            skLineSegment(sketch, "E875", {"start": v(5.16, -0.56) * mm, "end": v(5.38, -0.88) * mm});
            skLineSegment(sketch, "E876", {"start": v(5.38, -0.88) * mm, "end": v(5.47, -0.97) * mm});
            skLineSegment(sketch, "E877", {"start": v(5.47, -0.97) * mm, "end": v(5.47, -2.91) * mm});
            skLineSegment(sketch, "E878", {"start": v(5.47, -2.91) * mm, "end": v(5.65, -3.23) * mm});
            skLineSegment(sketch, "E879", {"start": v(5.65, -3.23) * mm, "end": v(5.83, -3.38) * mm});
            skLineSegment(sketch, "E880", {"start": v(5.83, -3.38) * mm, "end": v(5.95, -3.5) * mm});
            skLineSegment(sketch, "E881", {"start": v(5.95, -3.5) * mm, "end": v(5.56, -3.88) * mm});
            skLineSegment(sketch, "E882", {"start": v(5.56, -3.88) * mm, "end": v(5.58, -4.99) * mm});
            skLineSegment(sketch, "E883", {"start": v(5.58, -4.99) * mm, "end": v(5.72, -5.08) * mm});
            skLineSegment(sketch, "E884", {"start": v(5.72, -5.08) * mm, "end": v(5.77, -5.3) * mm});
            skLineSegment(sketch, "E885", {"start": v(5.77, -5.3) * mm, "end": v(5.77, -5.48) * mm});
            skLineSegment(sketch, "E886", {"start": v(5.77, -5.48) * mm, "end": v(6.04, -5.73) * mm});
            skLineSegment(sketch, "E887", {"start": v(6.04, -5.73) * mm, "end": v(5.97, -6.03) * mm});
            skLineSegment(sketch, "E888", {"start": v(5.97, -6.03) * mm, "end": v(6, -7.47) * mm});
            skLineSegment(sketch, "E889", {"start": v(6, -7.47) * mm, "end": v(6.3, -7.72) * mm});
            skLineSegment(sketch, "E890", {"start": v(6.3, -7.72) * mm, "end": v(6.67, -7.79) * mm});
            skLineSegment(sketch, "E891", {"start": v(6.67, -7.79) * mm, "end": v(6.94, -8.01) * mm});
            skLineSegment(sketch, "E892", {"start": v(6.94, -8.01) * mm, "end": v(7.4, -8.06) * mm});
            skLineSegment(sketch, "E893", {"start": v(7.4, -8.06) * mm, "end": v(7.6, -8.06) * mm});
            skLineSegment(sketch, "E894", {"start": v(7.6, -8.06) * mm, "end": v(7.93, -8.24) * mm});
            skLineSegment(sketch, "E895", {"start": v(7.93, -8.24) * mm, "end": v(8.02, -8.53) * mm});
            skLineSegment(sketch, "E896", {"start": v(8.02, -8.53) * mm, "end": v(7.93, -9) * mm});
            skLineSegment(sketch, "E897", {"start": v(7.93, -9) * mm, "end": v(7.84, -9.23) * mm});
            skLineSegment(sketch, "E898", {"start": v(7.84, -9.23) * mm, "end": v(7.35, -9.53) * mm});
            skLineSegment(sketch, "E899", {"start": v(7.35, -9.53) * mm, "end": v(7.21, -9.5) * mm});
            skLineSegment(sketch, "E900", {"start": v(7.21, -9.5) * mm, "end": v(7.03, -9.44) * mm});
            skLineSegment(sketch, "E901", {"start": v(7.03, -9.44) * mm, "end": v(6.85, -9.69) * mm});
            skLineSegment(sketch, "E902", {"start": v(6.85, -9.69) * mm, "end": v(6.04, -9.64) * mm});
            skLineSegment(sketch, "E903", {"start": v(6.04, -9.64) * mm, "end": v(5.72, -10) * mm});
            skLineSegment(sketch, "E904", {"start": v(5.72, -10) * mm, "end": v(3.69, -9.82) * mm});
            skLineSegment(sketch, "E905", {"start": v(3.69, -9.82) * mm, "end": v(3.26, -9.6) * mm});
            skLineSegment(sketch, "E906", {"start": v(3.26, -9.6) * mm, "end": v(2.97, -9.37) * mm});
            skLineSegment(sketch, "E907", {"start": v(2.97, -9.37) * mm, "end": v(2.78, -9.19) * mm});
            skLineSegment(sketch, "E908", {"start": v(2.78, -9.19) * mm, "end": v(2.74, -8.9) * mm});
            skLineSegment(sketch, "E909", {"start": v(2.74, -8.9) * mm, "end": v(2.7, -8.62) * mm});
            skLineSegment(sketch, "E910", {"start": v(2.7, -8.62) * mm, "end": v(3.1, -8.33) * mm});
            skLineSegment(sketch, "E911", {"start": v(3.1, -8.33) * mm, "end": v(3.55, -8.06) * mm});
            skLineSegment(sketch, "E912", {"start": v(3.55, -8.06) * mm, "end": v(4.23, -7.72) * mm});
            skLineSegment(sketch, "E913", {"start": v(4.23, -7.72) * mm, "end": v(4.41, -7.6) * mm});
            skLineSegment(sketch, "E914", {"start": v(4.41, -7.6) * mm, "end": v(4.68, -7.27) * mm});
            skLineSegment(sketch, "E915", {"start": v(4.68, -7.27) * mm, "end": v(4.95, -6.8) * mm});
            skLineSegment(sketch, "E916", {"start": v(4.95, -6.8) * mm, "end": v(4.68, -6.57) * mm});
            skLineSegment(sketch, "E917", {"start": v(4.68, -6.57) * mm, "end": v(4.5, -6.28) * mm});
            skLineSegment(sketch, "E918", {"start": v(4.5, -6.28) * mm, "end": v(4.32, -6) * mm});
            skLineSegment(sketch, "E919", {"start": v(4.23, -5.9) * mm, "end": v(4.68, -5.4) * mm});
            skLineSegment(sketch, "E920", {"start": v(4.68, -5.4) * mm, "end": v(4.9, -5.08) * mm});
            skLineSegment(sketch, "E921", {"start": v(4.9, -5.08) * mm, "end": v(4.95, -4.13) * mm});
            skLineSegment(sketch, "E922", {"start": v(4.95, -4.13) * mm, "end": v(4.61, -3.81) * mm});
            skLineSegment(sketch, "E923", {"start": v(4.61, -3.81) * mm, "end": v(4.86, -3.3) * mm});
            skLineSegment(sketch, "E924", {"start": v(4.86, -3.3) * mm, "end": v(4.9, -3.18) * mm});
            skLineSegment(sketch, "E925", {"start": v(4.9, -3.18) * mm, "end": v(5.09, -2.96) * mm});
            skLineSegment(sketch, "E926", {"start": v(5.09, -2.96) * mm, "end": v(5.04, -1.78) * mm});
            skLineSegment(sketch, "E927", {"start": v(5.04, -1.78) * mm, "end": v(4.98, -1.56) * mm});
            skLineSegment(sketch, "E928", {"start": v(4.98, -1.56) * mm, "end": v(4.67, -1.4) * mm});
            skLineSegment(sketch, "E929", {"start": v(4.67, -1.4) * mm, "end": v(4.34, -1.3) * mm});
            skLineSegment(sketch, "E930", {"start": v(4.34, -1.3) * mm, "end": v(4.05, -1.1) * mm});
            skLineSegment(sketch, "E931", {"start": v(4.05, -1.1) * mm, "end": v(3.9, -1.1) * mm});
            skLineSegment(sketch, "E932", {"start": v(3.9, -1.1) * mm, "end": v(3.6, -1.4) * mm});
            skLineSegment(sketch, "E933", {"start": v(3.6, -1.4) * mm, "end": v(3.35, -1.3) * mm});
            skLineSegment(sketch, "E934", {"start": v(3.35, -1.3) * mm, "end": v(4.05, -0.7) * mm});
            skLineSegment(sketch, "E935", {"start": v(4.05, -0.7) * mm, "end": v(3.9, 1.32) * mm});
            skLineSegment(sketch, "E936", {"start": v(23.22, -3.63) * mm, "end": v(22.65, -3.63) * mm});
            skLineSegment(sketch, "E937", {"start": v(22.65, -3.63) * mm, "end": v(22.32, -4.45) * mm});
            skLineSegment(sketch, "E938", {"start": v(22.32, -4.45) * mm, "end": v(21.98, -4.98) * mm});
            skLineSegment(sketch, "E939", {"start": v(21.98, -4.98) * mm, "end": v(21.53, -5.48) * mm});
            skLineSegment(sketch, "E940", {"start": v(21.53, -5.48) * mm, "end": v(20.97, -5.93) * mm});
            skLineSegment(sketch, "E941", {"start": v(20.97, -5.93) * mm, "end": v(20.97, -6.44) * mm});
            skLineSegment(sketch, "E942", {"start": v(20.97, -6.44) * mm, "end": v(20.97, -6.83) * mm});
            skLineSegment(sketch, "E943", {"start": v(20.97, -6.83) * mm, "end": v(21.65, -7.67) * mm});
            skLineSegment(sketch, "E944", {"start": v(21.65, -7.67) * mm, "end": v(22.1, -8.23) * mm});
            skLineSegment(sketch, "E945", {"start": v(22.1, -8.23) * mm, "end": v(21.59, -8.62) * mm});
            skLineSegment(sketch, "E946", {"start": v(21.59, -8.62) * mm, "end": v(21.36, -8.9) * mm});
            skLineSegment(sketch, "E947", {"start": v(21.36, -8.9) * mm, "end": v(21.65, -9.24) * mm});
            skLineSegment(sketch, "E948", {"start": v(21.65, -9.24) * mm, "end": v(21.9, -9.47) * mm});
            skLineSegment(sketch, "E949", {"start": v(21.9, -9.47) * mm, "end": v(22.35, -9.47) * mm});
            skLineSegment(sketch, "E950", {"start": v(22.35, -9.47) * mm, "end": v(22.9, -8.93) * mm});
            skLineSegment(sketch, "E951", {"start": v(22.9, -8.93) * mm, "end": v(22.82, -7.62) * mm});
            skLineSegment(sketch, "E952", {"start": v(22.82, -7.62) * mm, "end": v(23.16, -6.89) * mm});
            skLineSegment(sketch, "E953", {"start": v(23.16, -6.89) * mm, "end": v(23.36, -6.47) * mm});
            skLineSegment(sketch, "E954", {"start": v(23.36, -6.47) * mm, "end": v(23.72, -6.1) * mm});
            skLineSegment(sketch, "E955", {"start": v(23.72, -6.1) * mm, "end": v(24.11, -5.46) * mm});
            skLineSegment(sketch, "E956", {"start": v(24.11, -5.46) * mm, "end": v(23.66, -4.87) * mm});
            skLineSegment(sketch, "E957", {"start": v(23.66, -4.87) * mm, "end": v(23.22, -3.63) * mm});
            skLineSegment(sketch, "E958", {"start": v(20.07, -7.95) * mm, "end": v(21.08, -8.8) * mm});
            skLineSegment(sketch, "E959", {"start": v(21.08, -8.8) * mm, "end": v(21.08, -9.24) * mm});
            skLineSegment(sketch, "E960", {"start": v(21.08, -9.24) * mm, "end": v(20.64, -9.35) * mm});
            skLineSegment(sketch, "E961", {"start": v(20.64, -9.35) * mm, "end": v(20.86, -9.7) * mm});
            skLineSegment(sketch, "E962", {"start": v(20.86, -9.7) * mm, "end": v(20.47, -10.08) * mm});
            skLineSegment(sketch, "E963", {"start": v(20.47, -10.08) * mm, "end": v(19.85, -10.42) * mm});
            skLineSegment(sketch, "E964", {"start": v(19.85, -10.42) * mm, "end": v(19.54, -10.48) * mm});
            skLineSegment(sketch, "E965", {"start": v(19.54, -10.48) * mm, "end": v(19.29, -10.4) * mm});
            skLineSegment(sketch, "E966", {"start": v(19.29, -10.4) * mm, "end": v(18.84, -10.76) * mm});
            skLineSegment(sketch, "E967", {"start": v(18.84, -10.76) * mm, "end": v(17.97, -10.76) * mm});
            skLineSegment(sketch, "E968", {"start": v(17.97, -10.76) * mm, "end": v(17.3, -10.76) * mm});
            skLineSegment(sketch, "E969", {"start": v(17.3, -10.76) * mm, "end": v(15.7, -10.25) * mm});
            skLineSegment(sketch, "E970", {"start": v(15.7, -10.25) * mm, "end": v(15.05, -9.92) * mm});
            skLineSegment(sketch, "E971", {"start": v(15.05, -9.92) * mm, "end": v(14.8, -9.7) * mm});
            skLineSegment(sketch, "E972", {"start": v(14.8, -9.7) * mm, "end": v(14.02, -9.63) * mm});
            skLineSegment(sketch, "E973", {"start": v(14.02, -9.63) * mm, "end": v(13.46, -9.19) * mm});
            skLineSegment(sketch, "E974", {"start": v(13.46, -9.19) * mm, "end": v(13.34, -8.74) * mm});
            skLineSegment(sketch, "E975", {"start": v(13.34, -8.74) * mm, "end": v(12.56, -7.84) * mm});
            skLineSegment(sketch, "E976", {"start": v(12.56, -7.84) * mm, "end": v(12.03, -7.22) * mm});
            skLineSegment(sketch, "E977", {"start": v(12.03, -7.22) * mm, "end": v(11.6, -6.35) * mm});
            skLineSegment(sketch, "E978", {"start": v(11.6, -6.35) * mm, "end": v(11.66, -5.93) * mm});
            skLineSegment(sketch, "E979", {"start": v(11.66, -5.93) * mm, "end": v(11.44, -5.57) * mm});
            skLineSegment(sketch, "E980", {"start": v(11.44, -5.57) * mm, "end": v(11.77, -5.12) * mm});
            skLineSegment(sketch, "E981", {"start": v(11.77, -5.12) * mm, "end": v(11.21, -4.81) * mm});
            skLineSegment(sketch, "E982", {"start": v(11.21, -4.81) * mm, "end": v(11.1, -4.25) * mm});
            skLineSegment(sketch, "E983", {"start": v(11.1, -4.25) * mm, "end": v(11.32, -4.08) * mm});
            skLineSegment(sketch, "E984", {"start": v(11.32, -4.08) * mm, "end": v(10.88, -3.35) * mm});
            skLineSegment(sketch, "E985", {"start": v(10.88, -3.35) * mm, "end": v(10.54, -3.1) * mm});
            skLineSegment(sketch, "E986", {"start": v(10.54, -3.1) * mm, "end": v(11.1, -2.51) * mm});
            skLineSegment(sketch, "E987", {"start": v(11.1, -2.51) * mm, "end": v(11.1, -1.44) * mm});
            skLineSegment(sketch, "E988", {"start": v(11.1, -1.44) * mm, "end": v(10.82, -1.2) * mm});
            skLineSegment(sketch, "E989", {"start": v(10.82, -1.2) * mm, "end": v(10.6, -0.38) * mm});
            skLineSegment(sketch, "E990", {"start": v(10.6, -0.38) * mm, "end": v(10.82, 0.07) * mm});
            skLineSegment(sketch, "E991", {"start": v(10.82, 0.07) * mm, "end": v(11.04, 0.8) * mm});
            skLineSegment(sketch, "E992", {"start": v(11.04, 0.8) * mm, "end": v(11.38, 1.8) * mm});
            skLineSegment(sketch, "E993", {"start": v(11.38, 1.8) * mm, "end": v(11.5, 2.37) * mm});
            skLineSegment(sketch, "E994", {"start": v(11.5, 2.37) * mm, "end": v(11.88, 3.32) * mm});
            skLineSegment(sketch, "E995", {"start": v(11.88, 3.32) * mm, "end": v(12, 3.6) * mm});
            skLineSegment(sketch, "E996", {"start": v(12, 3.6) * mm, "end": v(12.33, 4.16) * mm});
            skLineSegment(sketch, "E997", {"start": v(12.33, 4.16) * mm, "end": v(12.73, 4.78) * mm});
            skLineSegment(sketch, "E998", {"start": v(12.73, 4.78) * mm, "end": v(13.12, 5.34) * mm});
            skLineSegment(sketch, "E999", {"start": v(13.12, 5.34) * mm, "end": v(13.8, 5.57) * mm});
            skLineSegment(sketch, "E1000", {"start": v(13.8, 5.57) * mm, "end": v(14.18, 5.73) * mm});
            skLineSegment(sketch, "E1001", {"start": v(14.18, 5.73) * mm, "end": v(14.8, 6.1) * mm});
            skLineSegment(sketch, "E1002", {"start": v(14.8, 6.1) * mm, "end": v(15.81, 6.58) * mm});
            skLineSegment(sketch, "E1003", {"start": v(15.81, 6.58) * mm, "end": v(16.15, 6.69) * mm});
            skLineSegment(sketch, "E1004", {"start": v(16.15, 6.69) * mm, "end": v(17.44, 6.86) * mm});
            skLineSegment(sketch, "E1005", {"start": v(17.44, 6.86) * mm, "end": v(17.55, 6.69) * mm});
            skLineSegment(sketch, "E1006", {"start": v(17.55, 6.69) * mm, "end": v(18.17, 6.44) * mm});
            skLineSegment(sketch, "E1007", {"start": v(18.17, 6.44) * mm, "end": v(18.84, 6.1) * mm});
            skLineSegment(sketch, "E1008", {"start": v(18.84, 6.1) * mm, "end": v(19.51, 5.96) * mm});
            skLineSegment(sketch, "E1009", {"start": v(20.1, 5.65) * mm, "end": v(20.64, 5.45) * mm});
            skLineSegment(sketch, "E1010", {"start": v(19.51, 5.96) * mm, "end": v(20.1, 5.65) * mm});
            skLineSegment(sketch, "E1011", {"start": v(20.64, 5.45) * mm, "end": v(21.1, 5.57) * mm});
            skLineSegment(sketch, "E1012", {"start": v(21.1, 5.57) * mm, "end": v(21.57, 5.5) * mm});
            skLineSegment(sketch, "E1013", {"start": v(21.57, 5.5) * mm, "end": v(21.8, 5.73) * mm});
            skLineSegment(sketch, "E1014", {"start": v(21.8, 5.73) * mm, "end": v(22.18, 5.7) * mm});
            skLineSegment(sketch, "E1015", {"start": v(22.18, 5.7) * mm, "end": v(22.24, 5.85) * mm});
            skLineSegment(sketch, "E1016", {"start": v(22.24, 5.85) * mm, "end": v(22.75, 5.9) * mm});
            skLineSegment(sketch, "E1017", {"start": v(22.75, 5.9) * mm, "end": v(22.8, 6.01) * mm});
            skLineSegment(sketch, "E1018", {"start": v(22.8, 6.01) * mm, "end": v(23.31, 5.85) * mm});
            skLineSegment(sketch, "E1019", {"start": v(23.31, 5.85) * mm, "end": v(23.75, 5.5) * mm});
            skLineSegment(sketch, "E1020", {"start": v(23.75, 5.5) * mm, "end": v(24.17, 5.05) * mm});
            skLineSegment(sketch, "E1021", {"start": v(24.17, 5.05) * mm, "end": v(24.2, 3.47) * mm});
            skLineSegment(sketch, "E1022", {"start": v(24.2, 3.47) * mm, "end": v(24.4, 3.32) * mm});
            skLineSegment(sketch, "E1023", {"start": v(24.4, 3.32) * mm, "end": v(24.35, 2.05) * mm});
            skLineSegment(sketch, "E1024", {"start": v(24.35, 2.05) * mm, "end": v(23.63, 1.5) * mm});
            skLineSegment(sketch, "E1025", {"start": v(23.63, 1.5) * mm, "end": v(23.51, 1.18) * mm});
            skLineSegment(sketch, "E1026", {"start": v(23.51, 1.18) * mm, "end": v(23.54, 0.73) * mm});
            skLineSegment(sketch, "E1027", {"start": v(23.54, 0.73) * mm, "end": v(23.5, 0.59) * mm});
            skLineSegment(sketch, "E1028", {"start": v(23.5, 0.59) * mm, "end": v(23.65, 0.37) * mm});
            skLineSegment(sketch, "E1029", {"start": v(23.65, 0.37) * mm, "end": v(23.76, -0.15) * mm});
            skLineSegment(sketch, "E1030", {"start": v(23.76, -0.15) * mm, "end": v(23.91, -0.37) * mm});
            skLineSegment(sketch, "E1031", {"start": v(23.91, -0.37) * mm, "end": v(23.84, -0.64) * mm});
            skLineSegment(sketch, "E1032", {"start": v(23.84, -0.64) * mm, "end": v(24.1, -0.77) * mm});
            skLineSegment(sketch, "E1033", {"start": v(24.1, -0.77) * mm, "end": v(24, -1) * mm});
            skLineSegment(sketch, "E1034", {"start": v(24, -1) * mm, "end": v(23.78, -1.2) * mm});
            skLineSegment(sketch, "E1035", {"start": v(23.78, -1.2) * mm, "end": v(23.76, -1.36) * mm});
            skLineSegment(sketch, "E1036", {"start": v(23.76, -1.36) * mm, "end": v(23.53, -1.51) * mm});
            skLineSegment(sketch, "E1037", {"start": v(23.53, -1.51) * mm, "end": v(23.3, -1.65) * mm});
            skLineSegment(sketch, "E1038", {"start": v(23.3, -1.65) * mm, "end": v(22.98, -1.47) * mm});
            skLineSegment(sketch, "E1039", {"start": v(22.98, -1.47) * mm, "end": v(22.47, -1.23) * mm});
            skLineSegment(sketch, "E1040", {"start": v(22.47, -1.23) * mm, "end": v(22.3, -0.85) * mm});
            skLineSegment(sketch, "E1041", {"start": v(22.3, -0.85) * mm, "end": v(22.2, -0.52) * mm});
            skLineSegment(sketch, "E1042", {"start": v(22.2, -0.52) * mm, "end": v(22.01, -0.25) * mm});
            skLineSegment(sketch, "E1043", {"start": v(22.01, -0.25) * mm, "end": v(21.96, -0.01) * mm});
            skLineSegment(sketch, "E1044", {"start": v(21.96, -0.01) * mm, "end": v(21.92, 0.23) * mm});
            skLineSegment(sketch, "E1045", {"start": v(21.92, 0.23) * mm, "end": v(21.73, 0.58) * mm});
            skLineSegment(sketch, "E1046", {"start": v(21.73, 0.58) * mm, "end": v(21.7, 0.77) * mm});
            skLineSegment(sketch, "E1047", {"start": v(21.7, 0.77) * mm, "end": v(21.39, 1.34) * mm});
            skLineSegment(sketch, "E1048", {"start": v(21.39, 1.34) * mm, "end": v(21.18, 1.58) * mm});
            skLineSegment(sketch, "E1049", {"start": v(21.18, 1.58) * mm, "end": v(20.95, 1.77) * mm});
            skLineSegment(sketch, "E1050", {"start": v(20.95, 1.77) * mm, "end": v(20.65, 1.98) * mm});
            skLineSegment(sketch, "E1051", {"start": v(20.65, 1.98) * mm, "end": v(20.19, 2.13) * mm});
            skLineSegment(sketch, "E1052", {"start": v(20.19, 2.13) * mm, "end": v(20.16, 2.57) * mm});
            skLineSegment(sketch, "E1053", {"start": v(20.16, 2.57) * mm, "end": v(19.8, 2.84) * mm});
            skLineSegment(sketch, "E1054", {"start": v(19.8, 2.84) * mm, "end": v(19.56, 2.99) * mm});
            skLineSegment(sketch, "E1055", {"start": v(19.56, 2.99) * mm, "end": v(19.42, 2.99) * mm});
            skLineSegment(sketch, "E1056", {"start": v(19.42, 2.99) * mm, "end": v(19.34, 3.1) * mm});
            skLineSegment(sketch, "E1057", {"start": v(19.34, 3.1) * mm, "end": v(17.64, 3.14) * mm});
            skLineSegment(sketch, "E1058", {"start": v(17.64, 3.14) * mm, "end": v(17.56, 3) * mm});
            skLineSegment(sketch, "E1059", {"start": v(17.56, 3) * mm, "end": v(17.5, 2.87) * mm});
            skLineSegment(sketch, "E1060", {"start": v(17.5, 2.87) * mm, "end": v(17.36, 2.68) * mm});
            skLineSegment(sketch, "E1061", {"start": v(17.36, 2.68) * mm, "end": v(17.27, 2.84) * mm});
            skLineSegment(sketch, "E1062", {"start": v(17.27, 2.84) * mm, "end": v(17.13, 2.84) * mm});
            skLineSegment(sketch, "E1063", {"start": v(17.13, 2.84) * mm, "end": v(17.1, 2) * mm});
            skLineSegment(sketch, "E1064", {"start": v(17.1, 2) * mm, "end": v(16.69, 1.75) * mm});
            skLineSegment(sketch, "E1065", {"start": v(16.69, 1.75) * mm, "end": v(16.6, 1.55) * mm});
            skLineSegment(sketch, "E1066", {"start": v(16.6, 1.55) * mm, "end": v(16.41, 1.58) * mm});
            skLineSegment(sketch, "E1067", {"start": v(16.41, 1.58) * mm, "end": v(16.38, 1.37) * mm});
            skLineSegment(sketch, "E1068", {"start": v(16.38, 1.37) * mm, "end": v(16.08, 1.1) * mm});
            skLineSegment(sketch, "E1069", {"start": v(16.08, 1.1) * mm, "end": v(15.85, 0.7) * mm});
            skLineSegment(sketch, "E1070", {"start": v(15.85, 0.7) * mm, "end": v(15.72, 0.44) * mm});
            skLineSegment(sketch, "E1071", {"start": v(15.72, 0.44) * mm, "end": v(15.58, 0.3) * mm});
            skLineSegment(sketch, "E1072", {"start": v(15.58, 0.3) * mm, "end": v(15.6, -0.35) * mm});
            skLineSegment(sketch, "E1073", {"start": v(15.6, -0.35) * mm, "end": v(15.34, -0.26) * mm});
            skLineSegment(sketch, "E1074", {"start": v(15.34, -0.26) * mm, "end": v(15.28, -0.05) * mm});
            skLineSegment(sketch, "E1075", {"start": v(15.28, -0.05) * mm, "end": v(15.1, 0.13) * mm});
            skLineSegment(sketch, "E1076", {"start": v(15.1, 0.13) * mm, "end": v(15.2, 0.36) * mm});
            skLineSegment(sketch, "E1077", {"start": v(15.2, 0.36) * mm, "end": v(15.32, 0.61) * mm});
            skLineSegment(sketch, "E1078", {"start": v(15.32, 0.61) * mm, "end": v(15.43, 0.7) * mm});
            skLineSegment(sketch, "E1079", {"start": v(15.43, 0.7) * mm, "end": v(15.48, 0.98) * mm});
            skLineSegment(sketch, "E1080", {"start": v(15.48, 0.98) * mm, "end": v(15.56, 1.15) * mm});
            skLineSegment(sketch, "E1081", {"start": v(15.56, 1.15) * mm, "end": v(15.74, 1.18) * mm});
            skLineSegment(sketch, "E1082", {"start": v(15.74, 1.18) * mm, "end": v(15.7, 1.47) * mm});
            skLineSegment(sketch, "E1083", {"start": v(15.7, 1.47) * mm, "end": v(15.25, 2.04) * mm});
            skLineSegment(sketch, "E1084", {"start": v(15.25, 2.04) * mm, "end": v(15.05, 2.02) * mm});
            skLineSegment(sketch, "E1085", {"start": v(15.05, 2.02) * mm, "end": v(14.86, 1.81) * mm});
            skLineSegment(sketch, "E1086", {"start": v(14.86, 1.81) * mm, "end": v(14.77, 1.5) * mm});
            skLineSegment(sketch, "E1087", {"start": v(14.77, 1.5) * mm, "end": v(14.88, 1.18) * mm});
            skLineSegment(sketch, "E1088", {"start": v(14.88, 1.18) * mm, "end": v(14.54, 0.63) * mm});
            skLineSegment(sketch, "E1089", {"start": v(14.54, 0.63) * mm, "end": v(14.4, 0.4) * mm});
            skLineSegment(sketch, "E1090", {"start": v(14.4, 0.4) * mm, "end": v(14.3, 0.3) * mm});
            skLineSegment(sketch, "E1091", {"start": v(14.3, 0.3) * mm, "end": v(14.03, 0.04) * mm});
            skLineSegment(sketch, "E1092", {"start": v(14.03, 0.04) * mm, "end": v(14.03, -0.86) * mm});
            skLineSegment(sketch, "E1093", {"start": v(14.03, -0.86) * mm, "end": v(14.3, -1.02) * mm});
            skLineSegment(sketch, "E1094", {"start": v(14.3, -1.02) * mm, "end": v(14.43, -1.08) * mm});
            skLineSegment(sketch, "E1095", {"start": v(14.43, -1.08) * mm, "end": v(14.83, -1.05) * mm});
            skLineSegment(sketch, "E1096", {"start": v(14.83, -1.05) * mm, "end": v(15.13, -1.02) * mm});
            skLineSegment(sketch, "E1097", {"start": v(15.13, -1.02) * mm, "end": v(15.43, -0.74) * mm});
            skLineSegment(sketch, "E1098", {"start": v(15.43, -0.74) * mm, "end": v(15.55, -0.9) * mm});
            skLineSegment(sketch, "E1099", {"start": v(15.55, -0.9) * mm, "end": v(15.53, -1.65) * mm});
            skLineSegment(sketch, "E1100", {"start": v(15.53, -1.65) * mm, "end": v(15.17, -1.34) * mm});
            skLineSegment(sketch, "E1101", {"start": v(15.17, -1.34) * mm, "end": v(15.01, -1.2) * mm});
            skLineSegment(sketch, "E1102", {"start": v(15.01, -1.2) * mm, "end": v(14.7, -1.38) * mm});
            skLineSegment(sketch, "E1103", {"start": v(14.7, -1.38) * mm, "end": v(14.39, -1.27) * mm});
            skLineSegment(sketch, "E1104", {"start": v(14.39, -1.27) * mm, "end": v(14.23, -1.19) * mm});
            skLineSegment(sketch, "E1105", {"start": v(14.23, -1.19) * mm, "end": v(14.07, -1.19) * mm});
            skLineSegment(sketch, "E1106", {"start": v(14.07, -1.19) * mm, "end": v(13.82, -1.42) * mm});
            skLineSegment(sketch, "E1107", {"start": v(13.82, -1.42) * mm, "end": v(13.73, -1.51) * mm});
            skLineSegment(sketch, "E1108", {"start": v(13.73, -1.51) * mm, "end": v(13.65, -1.66) * mm});
            skLineSegment(sketch, "E1109", {"start": v(13.65, -1.66) * mm, "end": v(13.57, -1.95) * mm});
            skLineSegment(sketch, "E1110", {"start": v(13.57, -1.95) * mm, "end": v(13.51, -3.38) * mm});
            skLineSegment(sketch, "E1111", {"start": v(13.51, -3.38) * mm, "end": v(13.75, -3.51) * mm});
            skLineSegment(sketch, "E1112", {"start": v(13.75, -3.51) * mm, "end": v(13.75, -3.9) * mm});
            skLineSegment(sketch, "E1113", {"start": v(13.75, -3.9) * mm, "end": v(13.54, -4) * mm});
            skLineSegment(sketch, "E1114", {"start": v(13.54, -4) * mm, "end": v(13.43, -4.33) * mm});
            skLineSegment(sketch, "E1115", {"start": v(13.43, -4.33) * mm, "end": v(13.94, -4.33) * mm});
            skLineSegment(sketch, "E1116", {"start": v(13.94, -4.33) * mm, "end": v(13.92, -4.48) * mm});
            skLineSegment(sketch, "E1117", {"start": v(13.92, -4.48) * mm, "end": v(13.3, -4.92) * mm});
            skLineSegment(sketch, "E1118", {"start": v(13.3, -4.92) * mm, "end": v(13.47, -5.24) * mm});
            skLineSegment(sketch, "E1119", {"start": v(13.47, -5.24) * mm, "end": v(13.65, -5.42) * mm});
            skLineSegment(sketch, "E1120", {"start": v(13.65, -5.42) * mm, "end": v(14.2, -6.25) * mm});
            skLineSegment(sketch, "E1121", {"start": v(14.2, -6.25) * mm, "end": v(14.69, -6.66) * mm});
            skLineSegment(sketch, "E1122", {"start": v(14.69, -6.66) * mm, "end": v(14.96, -6.95) * mm});
            skLineSegment(sketch, "E1123", {"start": v(14.96, -6.95) * mm, "end": v(15.37, -7.14) * mm});
            skLineSegment(sketch, "E1124", {"start": v(15.37, -7.14) * mm, "end": v(15.84, -7.32) * mm});
            skLineSegment(sketch, "E1125", {"start": v(15.84, -7.32) * mm, "end": v(16.02, -7.38) * mm});
            skLineSegment(sketch, "E1126", {"start": v(16.02, -7.38) * mm, "end": v(16.37, -7.52) * mm});
            skLineSegment(sketch, "E1127", {"start": v(16.37, -7.52) * mm, "end": v(16.8, -7.64) * mm});
            skLineSegment(sketch, "E1128", {"start": v(16.8, -7.64) * mm, "end": v(17.16, -7.76) * mm});
            skLineSegment(sketch, "E1129", {"start": v(17.16, -7.76) * mm, "end": v(17.4, -7.85) * mm});
            skLineSegment(sketch, "E1130", {"start": v(17.4, -7.85) * mm, "end": v(17.78, -7.88) * mm});
            skLineSegment(sketch, "E1131", {"start": v(17.78, -7.88) * mm, "end": v(18.13, -8.12) * mm});
            skLineSegment(sketch, "E1132", {"start": v(18.13, -8.12) * mm, "end": v(18.42, -8.14) * mm});
            skLineSegment(sketch, "E1133", {"start": v(18.42, -8.14) * mm, "end": v(18.9, -8.34) * mm});
            skLineSegment(sketch, "E1134", {"start": v(18.9, -8.34) * mm, "end": v(19.3, -8.6) * mm});
            skLineSegment(sketch, "E1135", {"start": v(19.3, -8.6) * mm, "end": v(19.7, -8.7) * mm});
            skLineSegment(sketch, "E1136", {"start": v(19.7, -8.7) * mm, "end": v(20.3, -8.99) * mm});
            skLineSegment(sketch, "E1137", {"start": v(20.3, -8.99) * mm, "end": v(20.41, -9.08) * mm});
            skLineSegment(sketch, "E1138", {"start": v(20.41, -9.08) * mm, "end": v(20.48, -8.94) * mm});
            skLineSegment(sketch, "E1139", {"start": v(20.48, -8.94) * mm, "end": v(20.41, -8.65) * mm});
            skLineSegment(sketch, "E1140", {"start": v(20.41, -8.65) * mm, "end": v(20.24, -8.42) * mm});
            skLineSegment(sketch, "E1141", {"start": v(20.24, -8.42) * mm, "end": v(19.97, -8.17) * mm});
            skLineSegment(sketch, "E1142", {"start": v(19.97, -8.17) * mm, "end": v(20.07, -7.95) * mm});
            skLineSegment(sketch, "E1143", {"start": v(-3.93, -8.82) * mm, "end": v(-3.93, -8.74) * mm});
            skLineSegment(sketch, "E1144", {"start": v(4.32, -6) * mm, "end": v(4.23, -5.9) * mm});
            skSolve(sketch);
        }
        {
            var Q0;
            Q0=qCreatedBy(makeId("Top.planeOp"),FACE);
            var sketch = newSketch(context, id + "F5", { "sketchPlane" : qUnion([Q0])});
            skLineSegment(sketch, "E1145", {"start": v(-17.5, -28.64) * mm, "end": v(-16.13, -28.64) * mm});
            skLineSegment(sketch, "E1146", {"start": v(-16.13, -28.64) * mm, "end": v(-15.97, -28.64) * mm});
            skLineSegment(sketch, "E1147", {"start": v(-15.97, -28.64) * mm, "end": v(-8, -28.64) * mm});
            skLineSegment(sketch, "E1148", {"start": v(-8, -28.64) * mm, "end": v(-8, -28.12) * mm});
            skLineSegment(sketch, "E1149", {"start": v(-8, -28.12) * mm, "end": v(-7.19, -28.12) * mm});
            skLineSegment(sketch, "E1150", {"start": v(-7.19, -28.12) * mm, "end": v(-6.94, -28.44) * mm});
            skLineSegment(sketch, "E1151", {"start": v(-6.94, -28.44) * mm, "end": v(-6.46, -28.44) * mm});
            skLineSegment(sketch, "E1152", {"start": v(-6.46, -28.44) * mm, "end": v(-5.74, -27.99) * mm});
            skLineSegment(sketch, "E1153", {"start": v(-5.74, -27.99) * mm, "end": v(-1.67, -27.99) * mm});
            skLineSegment(sketch, "E1154", {"start": v(-1.67, -27.99) * mm, "end": v(-1.34, -28.17) * mm});
            skLineSegment(sketch, "E1155", {"start": v(-1.34, -28.17) * mm, "end": v(0.83, -28.17) * mm});
            skLineSegment(sketch, "E1156", {"start": v(0.83, -28.17) * mm, "end": v(2.03, -28.35) * mm});
            skLineSegment(sketch, "E1157", {"start": v(2.03, -28.35) * mm, "end": v(4.1, -28.35) * mm});
            skLineSegment(sketch, "E1158", {"start": v(4.1, -28.35) * mm, "end": v(5.71, -28.35) * mm});
            skLineSegment(sketch, "E1159", {"start": v(5.71, -28.35) * mm, "end": v(5.94, -28.62) * mm});
            skLineSegment(sketch, "E1160", {"start": v(5.94, -28.62) * mm, "end": v(6.17, -28.42) * mm});
            skLineSegment(sketch, "E1161", {"start": v(6.17, -28.42) * mm, "end": v(7.09, -28.42) * mm});
            skLineSegment(sketch, "E1162", {"start": v(7.09, -28.42) * mm, "end": v(7.22, -28.54) * mm});
            skLineSegment(sketch, "E1163", {"start": v(7.22, -28.54) * mm, "end": v(14.22, -28.54) * mm});
            skLineSegment(sketch, "E1164", {"start": v(14.22, -28.54) * mm, "end": v(14.22, -28.33) * mm});
            skLineSegment(sketch, "E1165", {"start": v(14.22, -28.33) * mm, "end": v(14.93, -28.33) * mm});
            skLineSegment(sketch, "E1166", {"start": v(14.93, -28.33) * mm, "end": v(15.38, -28.24) * mm});
            skLineSegment(sketch, "E1167", {"start": v(15.38, -28.24) * mm, "end": v(15.38, -28.12) * mm});
            skLineSegment(sketch, "E1168", {"start": v(15.38, -28.12) * mm, "end": v(16.07, -28.12) * mm});
            skLineSegment(sketch, "E1169", {"start": v(16.07, -28.12) * mm, "end": v(16.07, -27.99) * mm});
            skLineSegment(sketch, "E1170", {"start": v(16.07, -27.99) * mm, "end": v(16.44, -27.99) * mm});
            skLineSegment(sketch, "E1171", {"start": v(16.44, -27.99) * mm, "end": v(16.44, -27.84) * mm});
            skLineSegment(sketch, "E1172", {"start": v(16.44, -27.84) * mm, "end": v(16.78, -28.05) * mm});
            skLineSegment(sketch, "E1173", {"start": v(16.78, -28.05) * mm, "end": v(17, -28.26) * mm});
            skLineSegment(sketch, "E1174", {"start": v(17, -28.26) * mm, "end": v(17, -28.54) * mm});
            skLineSegment(sketch, "E1175", {"start": v(17, -28.54) * mm, "end": v(17.2, -28.76) * mm});
            skLineSegment(sketch, "E1176", {"start": v(17.2, -28.76) * mm, "end": v(17.2, -29.06) * mm});
            skLineSegment(sketch, "E1177", {"start": v(17.2, -29.06) * mm, "end": v(17.2, -29.97) * mm});
            skLineSegment(sketch, "E1178", {"start": v(17.2, -29.97) * mm, "end": v(17.13, -30.12) * mm});
            skLineSegment(sketch, "E1179", {"start": v(17.13, -30.12) * mm, "end": v(17.05, -30.21) * mm});
            skLineSegment(sketch, "E1180", {"start": v(17.05, -30.21) * mm, "end": v(17, -30.35) * mm});
            skLineSegment(sketch, "E1181", {"start": v(17, -30.35) * mm, "end": v(16.88, -30.5) * mm});
            skLineSegment(sketch, "E1182", {"start": v(16.88, -30.5) * mm, "end": v(16.8, -30.72) * mm});
            skLineSegment(sketch, "E1183", {"start": v(16.8, -30.72) * mm, "end": v(16.7, -30.8) * mm});
            skLineSegment(sketch, "E1184", {"start": v(16.7, -30.8) * mm, "end": v(16.63, -30.6) * mm});
            skLineSegment(sketch, "E1185", {"start": v(16.63, -30.6) * mm, "end": v(16.55, -30.53) * mm});
            skLineSegment(sketch, "E1186", {"start": v(16.55, -30.53) * mm, "end": v(16.17, -30.53) * mm});
            skLineSegment(sketch, "E1187", {"start": v(16.17, -30.53) * mm, "end": v(16.17, -30.46) * mm});
            skLineSegment(sketch, "E1188", {"start": v(16.17, -30.46) * mm, "end": v(15.4, -30.46) * mm});
            skLineSegment(sketch, "E1189", {"start": v(15.4, -30.46) * mm, "end": v(15.4, -30.32) * mm});
            skLineSegment(sketch, "E1190", {"start": v(15.4, -30.32) * mm, "end": v(15.18, -30.25) * mm});
            skLineSegment(sketch, "E1191", {"start": v(15.18, -30.25) * mm, "end": v(15.02, -30.33) * mm});
            skLineSegment(sketch, "E1192", {"start": v(15.02, -30.33) * mm, "end": v(14.7, -30.24) * mm});
            skLineSegment(sketch, "E1193", {"start": v(14.7, -30.24) * mm, "end": v(14.5, -30.31) * mm});
            skLineSegment(sketch, "E1194", {"start": v(14.5, -30.31) * mm, "end": v(9.5, -30.25) * mm});
            skLineSegment(sketch, "E1195", {"start": v(9.5, -30.25) * mm, "end": v(9.46, -30.46) * mm});
            skLineSegment(sketch, "E1196", {"start": v(9.46, -30.46) * mm, "end": v(8.6, -30.45) * mm});
            skLineSegment(sketch, "E1197", {"start": v(8.6, -30.45) * mm, "end": v(8.56, -30.59) * mm});
            skLineSegment(sketch, "E1198", {"start": v(8.56, -30.59) * mm, "end": v(6.77, -30.56) * mm});
            skLineSegment(sketch, "E1199", {"start": v(6.77, -30.56) * mm, "end": v(6.77, -30.78) * mm});
            skLineSegment(sketch, "E1200", {"start": v(6.77, -30.78) * mm, "end": v(6.24, -30.77) * mm});
            skLineSegment(sketch, "E1201", {"start": v(6.24, -30.77) * mm, "end": v(6.13, -30.94) * mm});
            skLineSegment(sketch, "E1202", {"start": v(6.13, -30.94) * mm, "end": v(3.01, -30.9) * mm});
            skLineSegment(sketch, "E1203", {"start": v(3.01, -30.9) * mm, "end": v(2.88, -31.01) * mm});
            skLineSegment(sketch, "E1204", {"start": v(2.88, -31.01) * mm, "end": v(1.3, -31) * mm});
            skLineSegment(sketch, "E1205", {"start": v(1.3, -31) * mm, "end": v(1.3, -30.86) * mm});
            skLineSegment(sketch, "E1206", {"start": v(1.3, -30.86) * mm, "end": v(-0.84, -30.94) * mm});
            skLineSegment(sketch, "E1207", {"start": v(-0.84, -30.94) * mm, "end": v(-0.85, -30.77) * mm});
            skLineSegment(sketch, "E1208", {"start": v(-0.85, -30.77) * mm, "end": v(-1.58, -30.67) * mm});
            skLineSegment(sketch, "E1209", {"start": v(-1.58, -30.67) * mm, "end": v(-1.58, -30.95) * mm});
            skLineSegment(sketch, "E1210", {"start": v(-1.58, -30.95) * mm, "end": v(-5.08, -30.9) * mm});
            skLineSegment(sketch, "E1211", {"start": v(-5.08, -30.9) * mm, "end": v(-5.08, -30.7) * mm});
            skLineSegment(sketch, "E1212", {"start": v(-5.08, -30.7) * mm, "end": v(-5.58, -30.68) * mm});
            skLineSegment(sketch, "E1213", {"start": v(-5.58, -30.68) * mm, "end": v(-5.68, -30.59) * mm});
            skLineSegment(sketch, "E1214", {"start": v(-5.68, -30.59) * mm, "end": v(-5.96, -30.58) * mm});
            skLineSegment(sketch, "E1215", {"start": v(-5.96, -30.58) * mm, "end": v(-5.96, -30.25) * mm});
            skLineSegment(sketch, "E1216", {"start": v(-5.96, -30.25) * mm, "end": v(-6.38, -30.24) * mm});
            skLineSegment(sketch, "E1217", {"start": v(-6.38, -30.24) * mm, "end": v(-6.57, -30.08) * mm});
            skLineSegment(sketch, "E1218", {"start": v(-6.57, -30.08) * mm, "end": v(-6.75, -30.08) * mm});
            skLineSegment(sketch, "E1219", {"start": v(-6.75, -30.08) * mm, "end": v(-6.75, -30.25) * mm});
            skLineSegment(sketch, "E1220", {"start": v(-6.75, -30.25) * mm, "end": v(-6.99, -30.24) * mm});
            skLineSegment(sketch, "E1221", {"start": v(-6.99, -30.24) * mm, "end": v(-6.99, -30.47) * mm});
            skLineSegment(sketch, "E1222", {"start": v(-6.99, -30.47) * mm, "end": v(-7.13, -30.59) * mm});
            skLineSegment(sketch, "E1223", {"start": v(-7.13, -30.59) * mm, "end": v(-7.56, -30.58) * mm});
            skLineSegment(sketch, "E1224", {"start": v(-7.56, -30.58) * mm, "end": v(-7.73, -30.44) * mm});
            skLineSegment(sketch, "E1225", {"start": v(-7.86, -30.31) * mm, "end": v(-7.73, -30.44) * mm});
            skLineSegment(sketch, "E1226", {"start": v(-7.86, -30.31) * mm, "end": v(-8.32, -30.3) * mm});
            skLineSegment(sketch, "E1227", {"start": v(-8.32, -30.3) * mm, "end": v(-8.66, -30.3) * mm});
            skLineSegment(sketch, "E1228", {"start": v(-8.66, -30.3) * mm, "end": v(-8.66, -30.44) * mm});
            skLineSegment(sketch, "E1229", {"start": v(-8.66, -30.44) * mm, "end": v(-9, -30.36) * mm});
            skLineSegment(sketch, "E1230", {"start": v(-9, -30.36) * mm, "end": v(-9.26, -30.47) * mm});
            skLineSegment(sketch, "E1231", {"start": v(-9.26, -30.47) * mm, "end": v(-9.42, -30.45) * mm});
            skLineSegment(sketch, "E1232", {"start": v(-9.42, -30.45) * mm, "end": v(-9.57, -30.42) * mm});
            skLineSegment(sketch, "E1233", {"start": v(-9.57, -30.42) * mm, "end": v(-9.66, -30.53) * mm});
            skLineSegment(sketch, "E1234", {"start": v(-9.66, -30.53) * mm, "end": v(-9.93, -30.53) * mm});
            skLineSegment(sketch, "E1235", {"start": v(-9.93, -30.53) * mm, "end": v(-10.1, -30.74) * mm});
            skLineSegment(sketch, "E1236", {"start": v(-10.1, -30.74) * mm, "end": v(-10.3, -30.73) * mm});
            skLineSegment(sketch, "E1237", {"start": v(-10.3, -30.73) * mm, "end": v(-10.44, -30.59) * mm});
            skLineSegment(sketch, "E1238", {"start": v(-10.44, -30.59) * mm, "end": v(-10.58, -30.87) * mm});
            skLineSegment(sketch, "E1239", {"start": v(-10.58, -30.87) * mm, "end": v(-13.25, -30.83) * mm});
            skLineSegment(sketch, "E1240", {"start": v(-13.25, -30.83) * mm, "end": v(-13.46, -30.74) * mm});
            skLineSegment(sketch, "E1241", {"start": v(-13.46, -30.74) * mm, "end": v(-13.86, -30.73) * mm});
            skLineSegment(sketch, "E1242", {"start": v(-13.86, -30.73) * mm, "end": v(-13.86, -30.59) * mm});
            skLineSegment(sketch, "E1243", {"start": v(-13.86, -30.59) * mm, "end": v(-14.3, -30.58) * mm});
            skLineSegment(sketch, "E1244", {"start": v(-14.3, -30.58) * mm, "end": v(-14.4, -30.43) * mm});
            skLineSegment(sketch, "E1245", {"start": v(-14.4, -30.43) * mm, "end": v(-14.7, -30.43) * mm});
            skLineSegment(sketch, "E1246", {"start": v(-14.7, -30.43) * mm, "end": v(-14.81, -30.26) * mm});
            skLineSegment(sketch, "E1247", {"start": v(-14.81, -30.26) * mm, "end": v(-15.17, -30.1) * mm});
            skLineSegment(sketch, "E1248", {"start": v(-15.17, -30.1) * mm, "end": v(-15.51, -30.1) * mm});
            skLineSegment(sketch, "E1249", {"start": v(-15.51, -30.1) * mm, "end": v(-15.8, -29.96) * mm});
            skLineSegment(sketch, "E1250", {"start": v(-15.8, -29.96) * mm, "end": v(-16.25, -29.95) * mm});
            skLineSegment(sketch, "E1251", {"start": v(-16.25, -29.95) * mm, "end": v(-16.3, -29.7) * mm});
            skLineSegment(sketch, "E1252", {"start": v(-16.3, -29.7) * mm, "end": v(-16.62, -29.69) * mm});
            skLineSegment(sketch, "E1253", {"start": v(-16.62, -29.69) * mm, "end": v(-17.54, -28.91) * mm});
            skLineSegment(sketch, "E1254", {"start": v(-17.54, -28.91) * mm, "end": v(-17.5, -28.64) * mm});
            skSolve(sketch);
        }
        {
            var Q0;
            Q0 = qSketchRegion(id + "F0", true);
            extrude(context, id + "F6", {"entities" : qUnion([Q0]), "depth" : 6.35 * mm});
        }
        {
            var Q0;
            Q0 = qSketchRegion(id + "F1", true);
            extrude(context, id + "F7", {"entities" : qUnion([Q0]), "depth" : 9.52 * mm});
        }
        {
            var Q0;
            Q0 = qSketchRegion(id + "F2", true);
            extrude(context, id + "F8", {"entities" : qUnion([Q0]), "depth" : 11.9 * mm});
        }
        {
            var Q0;
            Q0 = qSketchRegion(id + "F3", true);
            extrude(context, id + "F9", {"entities" : qUnion([Q0]), "depth" : 11.9 * mm});
        }
        {
            var Q0;
            Q0 = qSketchRegion(id + "F4", true);
            extrude(context, id + "F10", {"entities" : qUnion([Q0]), "depth" : 12.7 * mm});
        }
        {
            var Q0;
            Q0 = qSketchRegion(id + "F5", true);
            extrude(context, id + "F11", {"entities" : qUnion([Q0]), "depth" : 11.9 * mm});
        }
    });
